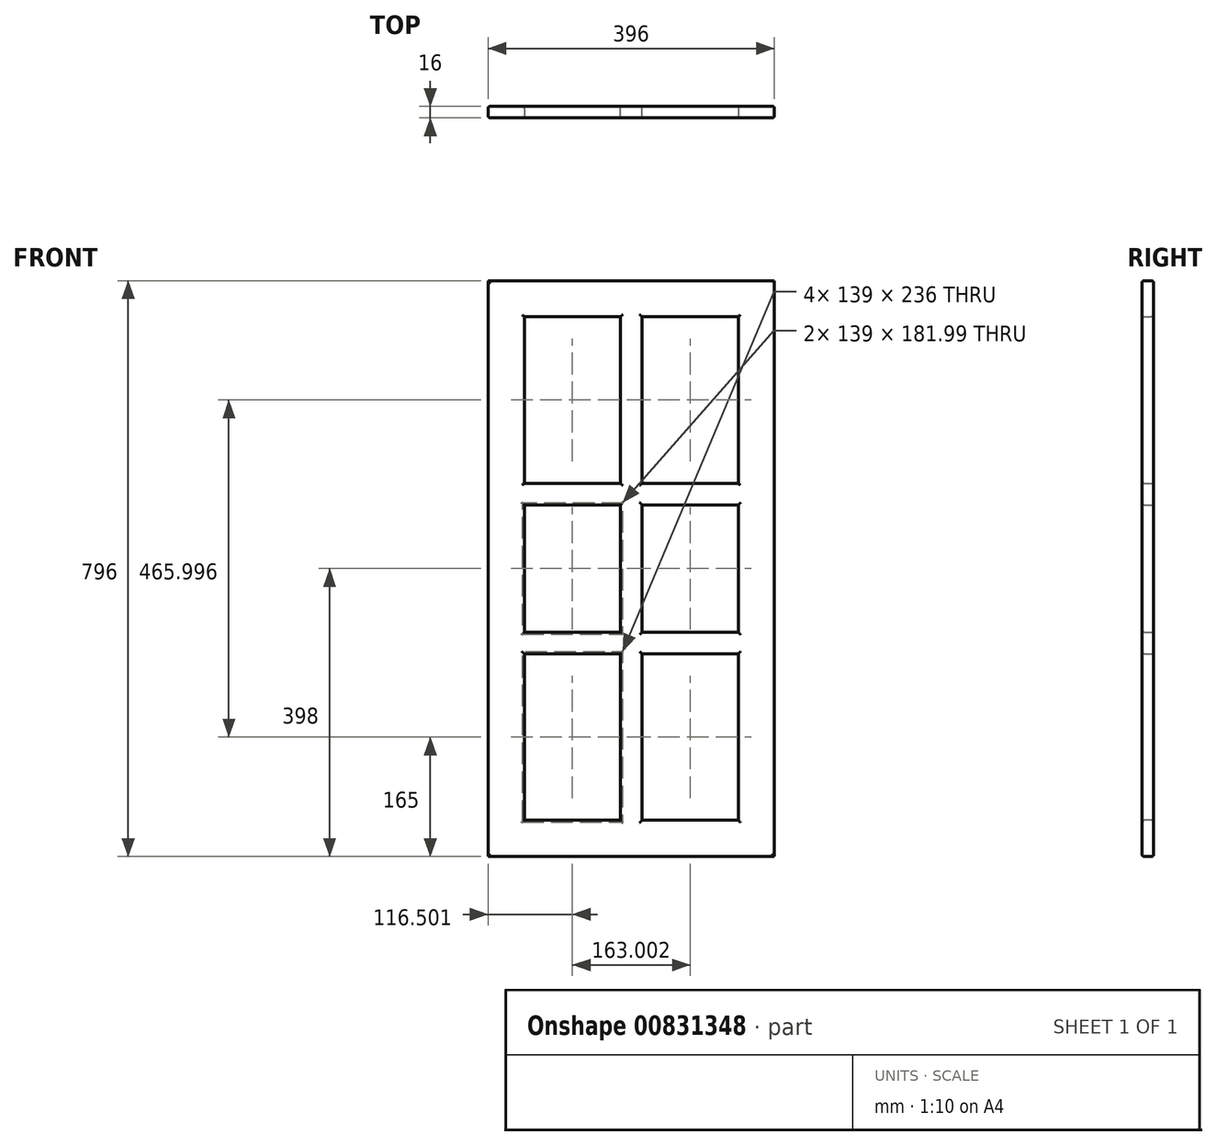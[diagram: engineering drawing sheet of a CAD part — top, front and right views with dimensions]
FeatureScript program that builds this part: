
annotation { "Feature Type Name" : "Feature", "Feature Type Description" : "" }
export const myFeature = defineFeature(function(context is Context, id is Id, definition is map)
    precondition{}
    {
        {
            var Q0;
            Q0=qCreatedBy(makeId("Front.planeOp"),FACE);
            var sketch = newSketch(context, id + "F0", { "sketchPlane" : qUnion([Q0])});
            skLineSegment(sketch, "E0.bottom", {"start": v(0, 0) * mm, "end": v(28.85, 0) * mm});
            skLineSegment(sketch, "E0.top", {"start": v(0, 37.88) * mm, "end": v(28.85, 37.88) * mm});
            skLineSegment(sketch, "E0.left", {"start": v(0, 0) * mm, "end": v(0, 37.88) * mm});
            skLineSegment(sketch, "E0.right", {"start": v(28.85, 0) * mm, "end": v(28.85, 37.88) * mm});
            skSolve(sketch);
        }
        {
            var Q0;
            Q0=makeQuery(id+"F0.imprint","IMPRINT",FACE,{"disambiguationData":[TD([[makeQuery(id+"F0.imprint","IMPRINT",EDGE,{"derivedFrom":sQuery(id+"F0.wireOp",EDGE,"E0.bottom")}),1.0]])]});
            extrude(context, id + "F1", {"entities" : qUnion([Q0]), "depth" : 16 * mm, "offsetDistance" : 25.4 * mm});
        }
        {
            var Q0;
            Q0=makeQuery(id+"F1.opExtrude","SWEPT_FACE",FACE,{"disambiguationData":[OSD([sQuery(id+"F0.wireOp",EDGE,"E0.left")])]});
            extrude(context, id + "F2", {"entities" : qUnion([Q0]), "operationType" : NewBodyOperationType.ADD, "oppositeDirection" : true, "depth" : 296 * mm, "offsetDistance" : 25.4 * mm});
        }
        {
            var Q0;
            {var subQ0=sQuery(id+"F0.wireOp",EDGE,"E0.bottom");Q0=makeQuery(id+"F2.boolean.opBoolean","MERGE",FACE,{"derivedFrom":[makeQuery(id+"F1.opExtrude","SWEPT_FACE",FACE,{"disambiguationData":[OSD([subQ0])]}),makeQuery(id+"F2.opExtrude","SWEPT_FACE",FACE,{"disambiguationData":[OSD([subQ0,sQuery(id+"F0.wireOp",EDGE,"E0.left")])]})]});}
            extrude(context, id + "F3", {"entities" : qUnion([Q0]), "operationType" : NewBodyOperationType.ADD, "oppositeDirection" : true, "depth" : 996 * mm, "offsetDistance" : 25 * mm});
        }
        {
            var Q0;
            {var subQ0=sQuery(id+"F0.wireOp",EDGE,"E0.left");var subQ1=sQuery(id+"F0.wireOp",EDGE,"E0.bottom");Q0=makeQuery(id+"F3.boolean.opBoolean","MERGE",FACE,{"derivedFrom":[makeQuery(id+"F2.boolean.opBoolean","MERGE",FACE,{"derivedFrom":[makeQuery(id+"F1.opExtrude","CAP_FACE",FACE,{"disambiguationData":[OSD([subQ1,sQuery(id+"F0.wireOp",EDGE,"E0.top"),subQ0,sQuery(id+"F0.wireOp",EDGE,"E0.right")])],"isStart":false}),makeQuery(id+"F2.opExtrude","SWEPT_FACE",FACE,{"disambiguationData":[OSD([subQ0]),TDD([makeQuery(id+"F1.opExtrude","CAP_EDGE",EDGE,{"disambiguationData":[OSD([subQ0])],"isStart":false})])]})]}),makeQuery(id+"F3.opExtrude","SWEPT_FACE",FACE,{"disambiguationData":[OSD([subQ1,subQ0]),TDD([makeQuery(id+"F2.boolean.opBoolean","MERGE",EDGE,{"derivedFrom":[makeQuery(id+"F1.opExtrude","CAP_EDGE",EDGE,{"disambiguationData":[OSD([subQ1])],"isStart":false}),makeQuery(id+"F2.opExtrude","SWEPT_EDGE",EDGE,{"disambiguationData":[OSD([subQ1,subQ0]),TDD([makeQuery(id+"F1.opExtrude","CAP_VERTEX",VERTEX,{"disambiguationData":[OSD([subQ1,subQ0])],"isStart":false})])]})]})])]})]});}
            var sketch = newSketch(context, id + "F4", { "sketchPlane" : qUnion([Q0])});
            skLineSegment(sketch, "E1.bottom", {"start": v(48.4, 906.79) * mm, "end": v(248.24, 906.79) * mm});
            skLineSegment(sketch, "E1.top", {"start": v(48.4, 105.66) * mm, "end": v(248.24, 105.66) * mm});
            skLineSegment(sketch, "E1.left", {"start": v(48.4, 906.79) * mm, "end": v(48.4, 105.66) * mm});
            skLineSegment(sketch, "E1.right", {"start": v(248.24, 906.79) * mm, "end": v(248.24, 105.66) * mm});
            skSolve(sketch);
        }
        {
            var Q0;
            Q0=makeQuery(id+"F4.imprint","IMPRINT",FACE,{"disambiguationData":[TD([[makeQuery(id+"F4.imprint","IMPRINT",EDGE,{"derivedFrom":sQuery(id+"F4.wireOp",EDGE,"E1.bottom")}),-1.0]])]});
            extrude(context, id + "F5", {"entities" : qUnion([Q0]), "operationType" : NewBodyOperationType.REMOVE, "oppositeDirection" : true, "depth" : 5 * mm, "offsetDistance" : 25 * mm});
        }
        {
            var Q0;
            Q0=makeQuery(id+"F5.boolean.opBoolean","COPY",FACE,{"derivedFrom":makeQuery(id+"F5.opExtrude","SWEPT_FACE",FACE,{"disambiguationData":[OSD([sQuery(id+"F4.wireOp",EDGE,"E1.bottom")])]})});
            extrude(context, id + "F6", {"entities" : qUnion([Q0]), "operationType" : NewBodyOperationType.REMOVE, "oppositeDirection" : true, "depth" : 39.2 * mm, "offsetDistance" : 25 * mm});
        }
        {
            var Q0;
            {var subQ0=sQuery(id+"F4.wireOp",EDGE,"E1.right");Q0=makeQuery(id+"F6.boolean.opBoolean","MERGE",FACE,{"derivedFrom":[makeQuery(id+"F5.boolean.opBoolean","COPY",FACE,{"derivedFrom":makeQuery(id+"F5.opExtrude","SWEPT_FACE",FACE,{"disambiguationData":[OSD([subQ0])]})}),makeQuery(id+"F6.opExtrude","SWEPT_FACE",FACE,{"disambiguationData":[OSD([sQuery(id+"F4.wireOp",EDGE,"E1.bottom"),subQ0])]})]});}
            extrude(context, id + "F7", {"entities" : qUnion([Q0]), "operationType" : NewBodyOperationType.ADD, "depth" : 2.24 * mm, "offsetDistance" : 25 * mm});
        }
        {
            var Q0;
            Q0=makeQuery(id+"F5.boolean.opBoolean","COPY",FACE,{"derivedFrom":makeQuery(id+"F5.opExtrude","SWEPT_FACE",FACE,{"disambiguationData":[OSD([sQuery(id+"F4.wireOp",EDGE,"E1.top")])]})});
            extrude(context, id + "F8", {"entities" : qUnion([Q0]), "operationType" : NewBodyOperationType.REMOVE, "oppositeDirection" : true, "depth" : 55.66 * mm, "offsetDistance" : 25 * mm});
        }
        {
            var Q0;
            {var subQ0=sQuery(id+"F4.wireOp",EDGE,"E1.left");Q0=makeQuery(id+"F8.boolean.opBoolean","MERGE",FACE,{"derivedFrom":[makeQuery(id+"F6.boolean.opBoolean","MERGE",FACE,{"derivedFrom":[makeQuery(id+"F5.boolean.opBoolean","COPY",FACE,{"derivedFrom":makeQuery(id+"F5.opExtrude","SWEPT_FACE",FACE,{"disambiguationData":[OSD([subQ0])]})}),makeQuery(id+"F6.opExtrude","SWEPT_FACE",FACE,{"disambiguationData":[OSD([sQuery(id+"F4.wireOp",EDGE,"E1.bottom"),subQ0])]})]}),makeQuery(id+"F8.opExtrude","SWEPT_FACE",FACE,{"disambiguationData":[OSD([sQuery(id+"F4.wireOp",EDGE,"E1.top"),subQ0])]})]});}
            extrude(context, id + "F9", {"entities" : qUnion([Q0]), "operationType" : NewBodyOperationType.ADD, "depth" : 1.59 * mm, "offsetDistance" : 25 * mm});
        }
        {
            var Q0;
            {var subQ0=sQuery(id+"F4.wireOp",EDGE,"E1.top");var subQ1=sQuery(id+"F4.wireOp",EDGE,"E1.bottom");Q0=makeQuery(id+"F8.boolean.opBoolean","MERGE",FACE,{"derivedFrom":[makeQuery(id+"F6.boolean.opBoolean","MERGE",FACE,{"derivedFrom":[makeQuery(id+"F5.boolean.opBoolean","COPY",FACE,{"derivedFrom":makeQuery(id+"F5.opExtrude","CAP_FACE",FACE,{"disambiguationData":[OSD([subQ1,subQ0,sQuery(id+"F4.wireOp",EDGE,"E1.left"),sQuery(id+"F4.wireOp",EDGE,"E1.right")])],"isStart":false})}),makeQuery(id+"F6.opExtrude","SWEPT_FACE",FACE,{"disambiguationData":[OSD([subQ1]),TDD([makeQuery(id+"F5.boolean.opBoolean","COPY",EDGE,{"derivedFrom":makeQuery(id+"F5.opExtrude","CAP_EDGE",EDGE,{"disambiguationData":[OSD([subQ1])],"isStart":false})})])]})]}),makeQuery(id+"F8.opExtrude","SWEPT_FACE",FACE,{"disambiguationData":[OSD([subQ0]),TDD([makeQuery(id+"F5.boolean.opBoolean","COPY",EDGE,{"derivedFrom":makeQuery(id+"F5.opExtrude","CAP_EDGE",EDGE,{"disambiguationData":[OSD([subQ0])],"isStart":false})})])]})]});}
            var sketch = newSketch(context, id + "F10", { "sketchPlane" : qUnion([Q0])});
            skLineSegment(sketch, "E2.bottom", {"start": v(127.14, 946) * mm, "end": v(181.91, 946) * mm});
            skLineSegment(sketch, "E2.top", {"start": v(127.14, 50) * mm, "end": v(181.91, 50) * mm});
            skLineSegment(sketch, "E2.left", {"start": v(127.14, 946) * mm, "end": v(127.14, 50) * mm});
            skLineSegment(sketch, "E2.right", {"start": v(181.91, 946) * mm, "end": v(181.91, 50) * mm});
            skSolve(sketch);
        }
        {
            var Q0;
            Q0=makeQuery(id+"F10.imprint","IMPRINT",FACE,{"disambiguationData":[TD([[makeQuery(id+"F10.imprint","IMPRINT",EDGE,{"derivedFrom":sQuery(id+"F10.wireOp",EDGE,"E2.bottom")}),-1.0]])]});
            extrude(context, id + "F11", {"entities" : qUnion([Q0]), "operationType" : NewBodyOperationType.ADD, "depth" : 5 * mm, "offsetDistance" : 25 * mm});
        }
        {
            var Q0;
            Q0=makeQuery(id+"F11.opExtrude","SWEPT_FACE",FACE,{"disambiguationData":[OSD([sQuery(id+"F10.wireOp",EDGE,"E2.left")])]});
            extrude(context, id + "F12", {"entities" : qUnion([Q0]), "operationType" : NewBodyOperationType.REMOVE, "oppositeDirection" : true, "depth" : 5.86 * mm, "offsetDistance" : 25 * mm});
        }
        {
            var Q0;
            Q0=makeQuery(id+"F11.opExtrude","SWEPT_FACE",FACE,{"disambiguationData":[OSD([sQuery(id+"F10.wireOp",EDGE,"E2.right")])]});
            extrude(context, id + "F13", {"entities" : qUnion([Q0]), "operationType" : NewBodyOperationType.REMOVE, "oppositeDirection" : true, "depth" : 18.91 * mm, "offsetDistance" : 25 * mm});
        }
        {
            var Q0;
            {var subQ0=sQuery(id+"F10.wireOp",EDGE,"E2.left");var subQ1=sQuery(id+"F4.wireOp",EDGE,"E1.bottom");var subQ2=sQuery(id+"F4.wireOp",EDGE,"E1.top");var subQ3=sQuery(id+"F4.wireOp",EDGE,"E1.left");Q0=makeQuery(id+"F12.boolean.opBoolean","MERGE",FACE,{"derivedFrom":[makeQuery(id+"F11.boolean.opBoolean","SPLIT",FACE,{"disambiguationData":[TD([makeQuery(id+"F11.opExtrude","SWEPT_FACE",FACE,{"disambiguationData":[OSD([subQ0])]})])],"derivedFrom":makeQuery(id+"F8.boolean.opBoolean","MERGE",FACE,{"derivedFrom":[makeQuery(id+"F6.boolean.opBoolean","MERGE",FACE,{"derivedFrom":[makeQuery(id+"F5.boolean.opBoolean","COPY",FACE,{"derivedFrom":makeQuery(id+"F5.opExtrude","CAP_FACE",FACE,{"disambiguationData":[OSD([subQ1,subQ2,subQ3,sQuery(id+"F4.wireOp",EDGE,"E1.right")])],"isStart":false})}),makeQuery(id+"F6.opExtrude","SWEPT_FACE",FACE,{"disambiguationData":[OSD([subQ1]),TDD([makeQuery(id+"F5.boolean.opBoolean","COPY",EDGE,{"derivedFrom":makeQuery(id+"F5.opExtrude","CAP_EDGE",EDGE,{"disambiguationData":[OSD([subQ1])],"isStart":false})})])]})]}),makeQuery(id+"F8.opExtrude","SWEPT_FACE",FACE,{"disambiguationData":[OSD([subQ2]),TDD([makeQuery(id+"F5.boolean.opBoolean","COPY",EDGE,{"derivedFrom":makeQuery(id+"F5.opExtrude","CAP_EDGE",EDGE,{"disambiguationData":[OSD([subQ2])],"isStart":false})})])]})]})}),makeQuery(id+"F12.opExtrude","SWEPT_FACE",FACE,{"disambiguationData":[OSD([subQ0]),TDD([makeQuery(id+"F11.opExtrude","CAP_EDGE",EDGE,{"disambiguationData":[OSD([subQ0])],"isStart":true})])]})]});}
            var sketch = newSketch(context, id + "F14", { "sketchPlane" : qUnion([Q0])});
            skLineSegment(sketch, "E3.bottom", {"start": v(50, 870.78) * mm, "end": v(133, 870.78) * mm});
            skLineSegment(sketch, "E3.top", {"start": v(50, 835.83) * mm, "end": v(133, 835.83) * mm});
            skLineSegment(sketch, "E3.left", {"start": v(50, 870.78) * mm, "end": v(50, 835.83) * mm});
            skLineSegment(sketch, "E3.right", {"start": v(133, 870.78) * mm, "end": v(133, 835.83) * mm});
            skLineSegment(sketch, "E4.bottom", {"start": v(50, 539.3) * mm, "end": v(133, 539.3) * mm});
            skLineSegment(sketch, "E4.top", {"start": v(50, 484.02) * mm, "end": v(133, 484.02) * mm});
            skLineSegment(sketch, "E4.left", {"start": v(50, 539.3) * mm, "end": v(50, 484.02) * mm});
            skLineSegment(sketch, "E4.right", {"start": v(133, 539.3) * mm, "end": v(133, 484.02) * mm});
            skSolve(sketch);
        }
        {
            var Q0;
            {var subQ0=sQuery(id+"F10.wireOp",EDGE,"E2.right");var subQ1=sQuery(id+"F4.wireOp",EDGE,"E1.top");var subQ2=sQuery(id+"F4.wireOp",EDGE,"E1.right");var subQ3=sQuery(id+"F4.wireOp",EDGE,"E1.bottom");Q0=makeQuery(id+"F13.boolean.opBoolean","MERGE",FACE,{"derivedFrom":[makeQuery(id+"F11.boolean.opBoolean","SPLIT",FACE,{"disambiguationData":[TD([makeQuery(id+"F11.opExtrude","SWEPT_FACE",FACE,{"disambiguationData":[OSD([subQ0])]})])],"derivedFrom":makeQuery(id+"F8.boolean.opBoolean","MERGE",FACE,{"derivedFrom":[makeQuery(id+"F6.boolean.opBoolean","MERGE",FACE,{"derivedFrom":[makeQuery(id+"F5.boolean.opBoolean","COPY",FACE,{"derivedFrom":makeQuery(id+"F5.opExtrude","CAP_FACE",FACE,{"disambiguationData":[OSD([subQ3,subQ1,sQuery(id+"F4.wireOp",EDGE,"E1.left"),subQ2])],"isStart":false})}),makeQuery(id+"F6.opExtrude","SWEPT_FACE",FACE,{"disambiguationData":[OSD([subQ3]),TDD([makeQuery(id+"F5.boolean.opBoolean","COPY",EDGE,{"derivedFrom":makeQuery(id+"F5.opExtrude","CAP_EDGE",EDGE,{"disambiguationData":[OSD([subQ3])],"isStart":false})})])]})]}),makeQuery(id+"F8.opExtrude","SWEPT_FACE",FACE,{"disambiguationData":[OSD([subQ1]),TDD([makeQuery(id+"F5.boolean.opBoolean","COPY",EDGE,{"derivedFrom":makeQuery(id+"F5.opExtrude","CAP_EDGE",EDGE,{"disambiguationData":[OSD([subQ1])],"isStart":false})})])]})]})}),makeQuery(id+"F13.opExtrude","SWEPT_FACE",FACE,{"disambiguationData":[OSD([subQ0]),TDD([makeQuery(id+"F11.opExtrude","CAP_EDGE",EDGE,{"disambiguationData":[OSD([subQ0])],"isStart":true})])]})]});}
            var sketch = newSketch(context, id + "F15", { "sketchPlane" : qUnion([Q0])});
            skLineSegment(sketch, "E5.bottom", {"start": v(163, 876.14) * mm, "end": v(246, 876.14) * mm});
            skLineSegment(sketch, "E5.top", {"start": v(163, 831.26) * mm, "end": v(246, 831.26) * mm});
            skLineSegment(sketch, "E5.left", {"start": v(163, 876.14) * mm, "end": v(163, 831.26) * mm});
            skLineSegment(sketch, "E5.right", {"start": v(246, 876.14) * mm, "end": v(246, 831.26) * mm});
            skLineSegment(sketch, "E6.bottom", {"start": v(163, 602.8) * mm, "end": v(246, 602.8) * mm});
            skLineSegment(sketch, "E6.top", {"start": v(163, 550.28) * mm, "end": v(246, 550.28) * mm});
            skLineSegment(sketch, "E6.left", {"start": v(163, 602.8) * mm, "end": v(163, 550.28) * mm});
            skLineSegment(sketch, "E6.right", {"start": v(246, 602.8) * mm, "end": v(246, 550.28) * mm});
            skSolve(sketch);
        }
        {
            var Q0;
            Q0=makeQuery(id+"F14.imprint","IMPRINT",FACE,{"disambiguationData":[TD([[makeQuery(id+"F14.imprint","IMPRINT",EDGE,{"derivedFrom":sQuery(id+"F14.wireOp",EDGE,"E3.bottom")}),-1.0]])]});
            var Q1;
            Q1=makeQuery(id+"F15.imprint","IMPRINT",FACE,{"disambiguationData":[TD([[makeQuery(id+"F15.imprint","IMPRINT",EDGE,{"derivedFrom":sQuery(id+"F15.wireOp",EDGE,"E5.bottom")}),-1.0]])]});
            var Q2;
            Q2=makeQuery(id+"F15.imprint","IMPRINT",FACE,{"disambiguationData":[TD([[makeQuery(id+"F15.imprint","IMPRINT",EDGE,{"derivedFrom":sQuery(id+"F15.wireOp",EDGE,"E6.bottom")}),-1.0]])]});
            var Q3;
            Q3=makeQuery(id+"F14.imprint","IMPRINT",FACE,{"disambiguationData":[TD([[makeQuery(id+"F14.imprint","IMPRINT",EDGE,{"derivedFrom":sQuery(id+"F14.wireOp",EDGE,"E4.bottom")}),-1.0]])]});
            extrude(context, id + "F16", {"entities" : qUnion([Q0, Q1, Q2, Q3]), "operationType" : NewBodyOperationType.ADD, "depth" : 5 * mm, "offsetDistance" : 25 * mm});
        }
        {
            var Q0;
            Q0=makeQuery(id+"F16.opExtrude","SWEPT_FACE",FACE,{"disambiguationData":[OSD([sQuery(id+"F15.wireOp",EDGE,"E6.top")])]});
            var Q1;
            Q1=makeQuery(id+"F16.opExtrude","SWEPT_FACE",FACE,{"disambiguationData":[OSD([sQuery(id+"F14.wireOp",EDGE,"E4.top")])]});
            extrude(context, id + "F17", {"entities" : qUnion([Q0, Q1]), "operationType" : NewBodyOperationType.ADD, "depth" : 300 * mm, "offsetDistance" : 25 * mm});
        }
        {
            var Q0;
            Q0=makeQuery(id+"F16.opExtrude","SWEPT_FACE",FACE,{"disambiguationData":[OSD([sQuery(id+"F14.wireOp",EDGE,"E4.bottom")])]});
            var Q1;
            Q1=makeQuery(id+"F16.opExtrude","SWEPT_FACE",FACE,{"disambiguationData":[OSD([sQuery(id+"F15.wireOp",EDGE,"E6.bottom")])]});
            extrude(context, id + "F18", {"entities" : qUnion([Q0, Q1]), "operationType" : NewBodyOperationType.REMOVE, "oppositeDirection" : true, "depth" : 300 * mm, "offsetDistance" : 25 * mm});
        }
        {
            var Q0;
            Q0=makeQuery(id+"F16.opExtrude","SWEPT_FACE",FACE,{"disambiguationData":[OSD([sQuery(id+"F14.wireOp",EDGE,"E3.top")])]});
            extrude(context, id + "F19", {"entities" : qUnion([Q0]), "operationType" : NewBodyOperationType.ADD, "depth" : 324.8 * mm, "offsetDistance" : 25 * mm});
        }
        {
            var Q0;
            Q0=makeQuery(id+"F16.opExtrude","SWEPT_FACE",FACE,{"disambiguationData":[OSD([sQuery(id+"F14.wireOp",EDGE,"E3.bottom")])]});
            extrude(context, id + "F20", {"entities" : qUnion([Q0]), "operationType" : NewBodyOperationType.REMOVE, "oppositeDirection" : true, "depth" : 324.8 * mm, "offsetDistance" : 25 * mm});
        }
        {
            var Q0;
            Q0=makeQuery(id+"F18.boolean.opBoolean","COPY",FACE,{"derivedFrom":makeQuery(id+"F18.opExtrude","CAP_FACE",FACE,{"disambiguationData":[OSD([sQuery(id+"F14.wireOp",EDGE,"E4.bottom")])],"isStart":false})});
            extrude(context, id + "F21", {"entities" : qUnion([Q0]), "operationType" : NewBodyOperationType.ADD, "depth" : 250 * mm, "offsetDistance" : 25 * mm});
        }
        {
            var Q0;
            Q0=makeQuery(id+"F17.opExtrude","CAP_FACE",FACE,{"disambiguationData":[OSD([sQuery(id+"F14.wireOp",EDGE,"E4.top")])],"isStart":false});
            extrude(context, id + "F22", {"entities" : qUnion([Q0]), "operationType" : NewBodyOperationType.REMOVE, "oppositeDirection" : true, "depth" : 250 * mm, "offsetDistance" : 25 * mm});
        }
        {
            var Q0;
            Q0=makeQuery(id+"F20.boolean.opBoolean","COPY",FACE,{"derivedFrom":makeQuery(id+"F20.opExtrude","CAP_FACE",FACE,{"disambiguationData":[OSD([sQuery(id+"F14.wireOp",EDGE,"E3.bottom")])],"isStart":false})});
            extrude(context, id + "F23", {"entities" : qUnion([Q0]), "operationType" : NewBodyOperationType.ADD, "depth" : 100 * mm, "offsetDistance" : 25 * mm});
        }
        {
            var Q0;
            Q0=makeQuery(id+"F19.opExtrude","CAP_FACE",FACE,{"disambiguationData":[OSD([sQuery(id+"F14.wireOp",EDGE,"E3.top")])],"isStart":false});
            extrude(context, id + "F24", {"entities" : qUnion([Q0]), "operationType" : NewBodyOperationType.REMOVE, "oppositeDirection" : true, "depth" : 100 * mm, "offsetDistance" : 25 * mm});
        }
        {
            var Q0;
            Q0=makeQuery(id+"F23.opExtrude","CAP_FACE",FACE,{"disambiguationData":[OSD([sQuery(id+"F14.wireOp",EDGE,"E3.bottom")])],"isStart":false});
            extrude(context, id + "F25", {"entities" : qUnion([Q0]), "operationType" : NewBodyOperationType.ADD, "depth" : 50 * mm, "offsetDistance" : 25 * mm});
        }
        {
            var Q0;
            Q0=makeQuery(id+"F24.boolean.opBoolean","COPY",FACE,{"derivedFrom":makeQuery(id+"F24.opExtrude","CAP_FACE",FACE,{"disambiguationData":[OSD([sQuery(id+"F14.wireOp",EDGE,"E3.top")])],"isStart":false})});
            extrude(context, id + "F26", {"entities" : qUnion([Q0]), "operationType" : NewBodyOperationType.REMOVE, "oppositeDirection" : true, "depth" : 50 * mm, "offsetDistance" : 25 * mm});
        }
        {
            var Q0;
            Q0=makeQuery(id+"F22.boolean.opBoolean","COPY",FACE,{"derivedFrom":makeQuery(id+"F22.opExtrude","CAP_FACE",FACE,{"disambiguationData":[OSD([sQuery(id+"F14.wireOp",EDGE,"E4.top")])],"isStart":false})});
            extrude(context, id + "F27", {"entities" : qUnion([Q0]), "operationType" : NewBodyOperationType.ADD, "depth" : 134.02 * mm, "offsetDistance" : 25 * mm});
        }
        {
            var Q0;
            Q0=makeQuery(id+"F27.opExtrude","CAP_FACE",FACE,{"disambiguationData":[OSD([sQuery(id+"F14.wireOp",EDGE,"E4.top")])],"isStart":false});
            extrude(context, id + "F28", {"entities" : qUnion([Q0]), "operationType" : NewBodyOperationType.REMOVE, "oppositeDirection" : true, "depth" : 100 * mm, "offsetDistance" : 25 * mm});
        }
        {
            var Q0;
            Q0=makeQuery(id+"F26.boolean.opBoolean","COPY",FACE,{"derivedFrom":makeQuery(id+"F26.opExtrude","CAP_FACE",FACE,{"disambiguationData":[OSD([sQuery(id+"F14.wireOp",EDGE,"E3.top")])],"isStart":false})});
            extrude(context, id + "F29", {"entities" : qUnion([Q0]), "operationType" : NewBodyOperationType.ADD, "depth" : 100 * mm, "offsetDistance" : 25 * mm});
        }
        {
            var Q0;
            Q0=makeQuery(id+"F25.opExtrude","CAP_FACE",FACE,{"disambiguationData":[OSD([sQuery(id+"F14.wireOp",EDGE,"E3.bottom")])],"isStart":false});
            extrude(context, id + "F30", {"entities" : qUnion([Q0]), "operationType" : NewBodyOperationType.REMOVE, "oppositeDirection" : true, "depth" : 100 * mm, "offsetDistance" : 25 * mm});
        }
        {
            var Q0;
            Q0=makeQuery(id+"F30.boolean.opBoolean","COPY",FACE,{"derivedFrom":makeQuery(id+"F30.opExtrude","CAP_FACE",FACE,{"disambiguationData":[OSD([sQuery(id+"F14.wireOp",EDGE,"E3.bottom")])],"isStart":false})});
            extrude(context, id + "F31", {"entities" : qUnion([Q0]), "operationType" : NewBodyOperationType.ADD, "depth" : 50 * mm, "offsetDistance" : 25 * mm});
        }
        {
            var Q0;
            Q0=makeQuery(id+"F29.opExtrude","CAP_FACE",FACE,{"disambiguationData":[OSD([sQuery(id+"F14.wireOp",EDGE,"E3.top")])],"isStart":false});
            extrude(context, id + "F32", {"entities" : qUnion([Q0]), "operationType" : NewBodyOperationType.REMOVE, "oppositeDirection" : true, "depth" : 54.95 * mm, "offsetDistance" : 25 * mm});
        }
        {
            var Q0;
            Q0=makeQuery(id+"F28.boolean.opBoolean","COPY",FACE,{"derivedFrom":makeQuery(id+"F28.opExtrude","CAP_FACE",FACE,{"disambiguationData":[OSD([sQuery(id+"F14.wireOp",EDGE,"E4.top")])],"isStart":false})});
            extrude(context, id + "F33", {"entities" : qUnion([Q0]), "operationType" : NewBodyOperationType.ADD, "depth" : 50 * mm, "offsetDistance" : 25 * mm});
        }
        {
            var Q0;
            Q0=makeQuery(id+"F21.opExtrude","CAP_FACE",FACE,{"disambiguationData":[OSD([sQuery(id+"F14.wireOp",EDGE,"E4.bottom")])],"isStart":false});
            extrude(context, id + "F34", {"entities" : qUnion([Q0]), "operationType" : NewBodyOperationType.REMOVE, "oppositeDirection" : true, "depth" : 109.3 * mm, "offsetDistance" : 25 * mm});
        }
        {
            var Q0;
            Q0=makeQuery(id+"F16.opExtrude","SWEPT_FACE",FACE,{"disambiguationData":[OSD([sQuery(id+"F15.wireOp",EDGE,"E5.top")])]});
            extrude(context, id + "F35", {"entities" : qUnion([Q0]), "operationType" : NewBodyOperationType.REMOVE, "oppositeDirection" : true, "depth" : 14.88 * mm, "offsetDistance" : 25 * mm});
        }
        {
            var Q0;
            Q0=makeQuery(id+"F35.boolean.opBoolean","COPY",FACE,{"derivedFrom":makeQuery(id+"F35.opExtrude","CAP_FACE",FACE,{"disambiguationData":[OSD([sQuery(id+"F15.wireOp",EDGE,"E5.top")])],"isStart":false})});
            extrude(context, id + "F36", {"entities" : qUnion([Q0]), "operationType" : NewBodyOperationType.ADD, "depth" : 230.15 * mm, "offsetDistance" : 25 * mm});
        }
        {
            var Q0;
            Q0=makeQuery(id+"F16.opExtrude","SWEPT_FACE",FACE,{"disambiguationData":[OSD([sQuery(id+"F15.wireOp",EDGE,"E5.bottom")])]});
            extrude(context, id + "F37", {"entities" : qUnion([Q0]), "operationType" : NewBodyOperationType.REMOVE, "oppositeDirection" : true, "depth" : 230.15 * mm, "offsetDistance" : 25 * mm});
        }
        {
            var Q0;
            Q0=makeQuery(id+"F17.opExtrude","CAP_FACE",FACE,{"disambiguationData":[OSD([sQuery(id+"F15.wireOp",EDGE,"E6.top")])],"isStart":false});
            extrude(context, id + "F38", {"entities" : qUnion([Q0]), "operationType" : NewBodyOperationType.REMOVE, "oppositeDirection" : true, "depth" : 22.52 * mm, "offsetDistance" : 25 * mm});
        }
        {
            var Q0;
            Q0=makeQuery(id+"F18.boolean.opBoolean","COPY",FACE,{"derivedFrom":makeQuery(id+"F18.opExtrude","CAP_FACE",FACE,{"disambiguationData":[OSD([sQuery(id+"F15.wireOp",EDGE,"E6.bottom")])],"isStart":false})});
            extrude(context, id + "F39", {"entities" : qUnion([Q0]), "operationType" : NewBodyOperationType.ADD, "depth" : 77.2 * mm, "offsetDistance" : 25 * mm});
        }
        {
            var Q0;
            Q0=makeQuery(id+"F38.boolean.opBoolean","COPY",FACE,{"derivedFrom":makeQuery(id+"F38.opExtrude","CAP_FACE",FACE,{"disambiguationData":[OSD([sQuery(id+"F15.wireOp",EDGE,"E6.top")])],"isStart":false})});
            extrude(context, id + "F40", {"entities" : qUnion([Q0]), "operationType" : NewBodyOperationType.REMOVE, "oppositeDirection" : true, "depth" : 77.2 * mm, "offsetDistance" : 25 * mm});
        }
        {
            var Q0;
            {var subQ0=sQuery(id+"F14.wireOp",EDGE,"E3.bottom");var subQ1=makeQuery(id+"F16.opExtrude","CAP_EDGE",EDGE,{"disambiguationData":[OSD([subQ0])],"isStart":true});var subQ2=sQuery(id+"F10.wireOp",EDGE,"E2.left");var subQ3=sQuery(id+"F4.wireOp",EDGE,"E1.bottom");var subQ4=sQuery(id+"F4.wireOp",EDGE,"E1.left");var subQ5=sQuery(id+"F4.wireOp",EDGE,"E1.top");var subQ7=makeQuery(id+"F6.boolean.opBoolean","COPY",FACE,{"derivedFrom":makeQuery(id+"F6.opExtrude","CAP_FACE",FACE,{"disambiguationData":[OSD([subQ3])],"isStart":false})});Q0=makeQuery(id+"F30.boolean.opBoolean","MERGE",FACE,{"derivedFrom":[makeQuery(id+"F20.boolean.opBoolean","MERGE",FACE,{"derivedFrom":[makeQuery(id+"F16.boolean.opBoolean","SPLIT",FACE,{"disambiguationData":[TD([subQ7])],"derivedFrom":makeQuery(id+"F12.boolean.opBoolean","MERGE",FACE,{"derivedFrom":[makeQuery(id+"F11.boolean.opBoolean","SPLIT",FACE,{"disambiguationData":[TD([makeQuery(id+"F11.opExtrude","SWEPT_FACE",FACE,{"disambiguationData":[OSD([subQ2])]})])],"derivedFrom":makeQuery(id+"F8.boolean.opBoolean","MERGE",FACE,{"derivedFrom":[makeQuery(id+"F6.boolean.opBoolean","MERGE",FACE,{"derivedFrom":[makeQuery(id+"F5.boolean.opBoolean","COPY",FACE,{"derivedFrom":makeQuery(id+"F5.opExtrude","CAP_FACE",FACE,{"disambiguationData":[OSD([subQ3,subQ5,subQ4,sQuery(id+"F4.wireOp",EDGE,"E1.right")])],"isStart":false})}),makeQuery(id+"F6.opExtrude","SWEPT_FACE",FACE,{"disambiguationData":[OSD([subQ3]),TDD([makeQuery(id+"F5.boolean.opBoolean","COPY",EDGE,{"derivedFrom":makeQuery(id+"F5.opExtrude","CAP_EDGE",EDGE,{"disambiguationData":[OSD([subQ3])],"isStart":false})})])]})]}),makeQuery(id+"F8.opExtrude","SWEPT_FACE",FACE,{"disambiguationData":[OSD([subQ5]),TDD([makeQuery(id+"F5.boolean.opBoolean","COPY",EDGE,{"derivedFrom":makeQuery(id+"F5.opExtrude","CAP_EDGE",EDGE,{"disambiguationData":[OSD([subQ5])],"isStart":false})})])]})]})}),makeQuery(id+"F12.opExtrude","SWEPT_FACE",FACE,{"disambiguationData":[OSD([subQ2]),TDD([makeQuery(id+"F11.opExtrude","CAP_EDGE",EDGE,{"disambiguationData":[OSD([subQ2])],"isStart":true})])]})]})}),makeQuery(id+"F20.opExtrude","SWEPT_FACE",FACE,{"disambiguationData":[OSD([subQ0]),TDD([subQ1])]})]}),makeQuery(id+"F30.opExtrude","SWEPT_FACE",FACE,{"disambiguationData":[OSD([subQ0]),TDD([makeQuery(id+"F25.opExtrude","CAP_EDGE",EDGE,{"disambiguationData":[OSD([subQ0]),TDD([makeQuery(id+"F23.opExtrude","CAP_EDGE",EDGE,{"disambiguationData":[OSD([subQ0]),TDD([makeQuery(id+"F20.boolean.opBoolean","COPY",EDGE,{"derivedFrom":makeQuery(id+"F20.opExtrude","CAP_EDGE",EDGE,{"disambiguationData":[OSD([subQ0]),TDD([subQ1])],"isStart":false})})])],"isStart":false})])],"isStart":false})])]})]});}
            var Q1;
            {var subQ0=sQuery(id+"F15.wireOp",EDGE,"E5.bottom");var subQ1=sQuery(id+"F10.wireOp",EDGE,"E2.right");var subQ2=sQuery(id+"F4.wireOp",EDGE,"E1.bottom");var subQ3=sQuery(id+"F4.wireOp",EDGE,"E1.right");var subQ4=sQuery(id+"F4.wireOp",EDGE,"E1.top");var subQ7=makeQuery(id+"F6.boolean.opBoolean","COPY",FACE,{"derivedFrom":makeQuery(id+"F6.opExtrude","CAP_FACE",FACE,{"disambiguationData":[OSD([subQ2])],"isStart":false})});Q1=makeQuery(id+"F37.boolean.opBoolean","MERGE",FACE,{"derivedFrom":[makeQuery(id+"F16.boolean.opBoolean","SPLIT",FACE,{"disambiguationData":[TD([subQ7])],"derivedFrom":makeQuery(id+"F13.boolean.opBoolean","MERGE",FACE,{"derivedFrom":[makeQuery(id+"F11.boolean.opBoolean","SPLIT",FACE,{"disambiguationData":[TD([makeQuery(id+"F11.opExtrude","SWEPT_FACE",FACE,{"disambiguationData":[OSD([subQ1])]})])],"derivedFrom":makeQuery(id+"F8.boolean.opBoolean","MERGE",FACE,{"derivedFrom":[makeQuery(id+"F6.boolean.opBoolean","MERGE",FACE,{"derivedFrom":[makeQuery(id+"F5.boolean.opBoolean","COPY",FACE,{"derivedFrom":makeQuery(id+"F5.opExtrude","CAP_FACE",FACE,{"disambiguationData":[OSD([subQ2,subQ4,sQuery(id+"F4.wireOp",EDGE,"E1.left"),subQ3])],"isStart":false})}),makeQuery(id+"F6.opExtrude","SWEPT_FACE",FACE,{"disambiguationData":[OSD([subQ2]),TDD([makeQuery(id+"F5.boolean.opBoolean","COPY",EDGE,{"derivedFrom":makeQuery(id+"F5.opExtrude","CAP_EDGE",EDGE,{"disambiguationData":[OSD([subQ2])],"isStart":false})})])]})]}),makeQuery(id+"F8.opExtrude","SWEPT_FACE",FACE,{"disambiguationData":[OSD([subQ4]),TDD([makeQuery(id+"F5.boolean.opBoolean","COPY",EDGE,{"derivedFrom":makeQuery(id+"F5.opExtrude","CAP_EDGE",EDGE,{"disambiguationData":[OSD([subQ4])],"isStart":false})})])]})]})}),makeQuery(id+"F13.opExtrude","SWEPT_FACE",FACE,{"disambiguationData":[OSD([subQ1]),TDD([makeQuery(id+"F11.opExtrude","CAP_EDGE",EDGE,{"disambiguationData":[OSD([subQ1])],"isStart":true})])]})]})}),makeQuery(id+"F37.opExtrude","SWEPT_FACE",FACE,{"disambiguationData":[OSD([subQ0]),TDD([makeQuery(id+"F16.opExtrude","CAP_EDGE",EDGE,{"disambiguationData":[OSD([subQ0])],"isStart":true})])]})]});}
            var Q2;
            {var subQ0=sQuery(id+"F15.wireOp",EDGE,"E5.top");var subQ1=sQuery(id+"F15.wireOp",EDGE,"E6.bottom");var subQ2=sQuery(id+"F10.wireOp",EDGE,"E2.right");var subQ3=sQuery(id+"F4.wireOp",EDGE,"E1.right");var subQ4=sQuery(id+"F4.wireOp",EDGE,"E1.top");var subQ6=sQuery(id+"F4.wireOp",EDGE,"E1.bottom");Q2=makeQuery(id+"F35.boolean.opBoolean","MERGE",FACE,{"derivedFrom":[makeQuery(id+"F18.boolean.opBoolean","MERGE",FACE,{"derivedFrom":[makeQuery(id+"F16.boolean.opBoolean","SPLIT",FACE,{"disambiguationData":[TD([makeQuery(id+"F16.opExtrude","SWEPT_FACE",FACE,{"disambiguationData":[OSD([subQ0])]})])],"derivedFrom":makeQuery(id+"F13.boolean.opBoolean","MERGE",FACE,{"derivedFrom":[makeQuery(id+"F11.boolean.opBoolean","SPLIT",FACE,{"disambiguationData":[TD([makeQuery(id+"F11.opExtrude","SWEPT_FACE",FACE,{"disambiguationData":[OSD([subQ2])]})])],"derivedFrom":makeQuery(id+"F8.boolean.opBoolean","MERGE",FACE,{"derivedFrom":[makeQuery(id+"F6.boolean.opBoolean","MERGE",FACE,{"derivedFrom":[makeQuery(id+"F5.boolean.opBoolean","COPY",FACE,{"derivedFrom":makeQuery(id+"F5.opExtrude","CAP_FACE",FACE,{"disambiguationData":[OSD([subQ6,subQ4,sQuery(id+"F4.wireOp",EDGE,"E1.left"),subQ3])],"isStart":false})}),makeQuery(id+"F6.opExtrude","SWEPT_FACE",FACE,{"disambiguationData":[OSD([subQ6]),TDD([makeQuery(id+"F5.boolean.opBoolean","COPY",EDGE,{"derivedFrom":makeQuery(id+"F5.opExtrude","CAP_EDGE",EDGE,{"disambiguationData":[OSD([subQ6])],"isStart":false})})])]})]}),makeQuery(id+"F8.opExtrude","SWEPT_FACE",FACE,{"disambiguationData":[OSD([subQ4]),TDD([makeQuery(id+"F5.boolean.opBoolean","COPY",EDGE,{"derivedFrom":makeQuery(id+"F5.opExtrude","CAP_EDGE",EDGE,{"disambiguationData":[OSD([subQ4])],"isStart":false})})])]})]})}),makeQuery(id+"F13.opExtrude","SWEPT_FACE",FACE,{"disambiguationData":[OSD([subQ2]),TDD([makeQuery(id+"F11.opExtrude","CAP_EDGE",EDGE,{"disambiguationData":[OSD([subQ2])],"isStart":true})])]})]})}),makeQuery(id+"F18.opExtrude","SWEPT_FACE",FACE,{"disambiguationData":[OSD([subQ1]),TDD([makeQuery(id+"F16.opExtrude","CAP_EDGE",EDGE,{"disambiguationData":[OSD([subQ1])],"isStart":true})])]})]}),makeQuery(id+"F35.opExtrude","SWEPT_FACE",FACE,{"disambiguationData":[OSD([subQ0]),TDD([makeQuery(id+"F16.opExtrude","CAP_EDGE",EDGE,{"disambiguationData":[OSD([subQ0])],"isStart":true})])]})]});}
            var Q3;
            {var subQ0=sQuery(id+"F14.wireOp",EDGE,"E4.bottom");var subQ1=makeQuery(id+"F16.opExtrude","CAP_EDGE",EDGE,{"disambiguationData":[OSD([subQ0])],"isStart":true});var subQ2=sQuery(id+"F14.wireOp",EDGE,"E3.top");var subQ3=makeQuery(id+"F19.opExtrude","CAP_EDGE",EDGE,{"disambiguationData":[OSD([subQ2]),TDD([makeQuery(id+"F16.opExtrude","CAP_EDGE",EDGE,{"disambiguationData":[OSD([subQ2])],"isStart":true})])],"isStart":false});var subQ4=makeQuery(id+"F24.boolean.opBoolean","COPY",EDGE,{"derivedFrom":makeQuery(id+"F24.opExtrude","CAP_EDGE",EDGE,{"disambiguationData":[OSD([subQ2]),TDD([subQ3])],"isStart":false})});var subQ5=sQuery(id+"F4.wireOp",EDGE,"E1.left");var subQ6=sQuery(id+"F4.wireOp",EDGE,"E1.top");var subQ7=sQuery(id+"F4.wireOp",EDGE,"E1.bottom");var subQ9=sQuery(id+"F10.wireOp",EDGE,"E2.left");Q3=makeQuery(id+"F34.boolean.opBoolean","MERGE",FACE,{"derivedFrom":[makeQuery(id+"F32.boolean.opBoolean","MERGE",FACE,{"derivedFrom":[makeQuery(id+"F26.boolean.opBoolean","MERGE",FACE,{"derivedFrom":[makeQuery(id+"F24.boolean.opBoolean","MERGE",FACE,{"derivedFrom":[makeQuery(id+"F18.boolean.opBoolean","MERGE",FACE,{"derivedFrom":[makeQuery(id+"F16.boolean.opBoolean","SPLIT",FACE,{"disambiguationData":[TD([makeQuery(id+"F16.opExtrude","SWEPT_FACE",FACE,{"disambiguationData":[OSD([subQ2])]})])],"derivedFrom":makeQuery(id+"F12.boolean.opBoolean","MERGE",FACE,{"derivedFrom":[makeQuery(id+"F11.boolean.opBoolean","SPLIT",FACE,{"disambiguationData":[TD([makeQuery(id+"F11.opExtrude","SWEPT_FACE",FACE,{"disambiguationData":[OSD([subQ9])]})])],"derivedFrom":makeQuery(id+"F8.boolean.opBoolean","MERGE",FACE,{"derivedFrom":[makeQuery(id+"F6.boolean.opBoolean","MERGE",FACE,{"derivedFrom":[makeQuery(id+"F5.boolean.opBoolean","COPY",FACE,{"derivedFrom":makeQuery(id+"F5.opExtrude","CAP_FACE",FACE,{"disambiguationData":[OSD([subQ7,subQ6,subQ5,sQuery(id+"F4.wireOp",EDGE,"E1.right")])],"isStart":false})}),makeQuery(id+"F6.opExtrude","SWEPT_FACE",FACE,{"disambiguationData":[OSD([subQ7]),TDD([makeQuery(id+"F5.boolean.opBoolean","COPY",EDGE,{"derivedFrom":makeQuery(id+"F5.opExtrude","CAP_EDGE",EDGE,{"disambiguationData":[OSD([subQ7])],"isStart":false})})])]})]}),makeQuery(id+"F8.opExtrude","SWEPT_FACE",FACE,{"disambiguationData":[OSD([subQ6]),TDD([makeQuery(id+"F5.boolean.opBoolean","COPY",EDGE,{"derivedFrom":makeQuery(id+"F5.opExtrude","CAP_EDGE",EDGE,{"disambiguationData":[OSD([subQ6])],"isStart":false})})])]})]})}),makeQuery(id+"F12.opExtrude","SWEPT_FACE",FACE,{"disambiguationData":[OSD([subQ9]),TDD([makeQuery(id+"F11.opExtrude","CAP_EDGE",EDGE,{"disambiguationData":[OSD([subQ9])],"isStart":true})])]})]})}),makeQuery(id+"F18.opExtrude","SWEPT_FACE",FACE,{"disambiguationData":[OSD([subQ0]),TDD([subQ1])]})]}),makeQuery(id+"F24.opExtrude","SWEPT_FACE",FACE,{"disambiguationData":[OSD([subQ2]),TDD([subQ3])]})]}),makeQuery(id+"F26.opExtrude","SWEPT_FACE",FACE,{"disambiguationData":[OSD([subQ2]),TDD([subQ4])]})]}),makeQuery(id+"F32.opExtrude","SWEPT_FACE",FACE,{"disambiguationData":[OSD([subQ2]),TDD([makeQuery(id+"F29.opExtrude","CAP_EDGE",EDGE,{"disambiguationData":[OSD([subQ2]),TDD([makeQuery(id+"F26.boolean.opBoolean","COPY",EDGE,{"derivedFrom":makeQuery(id+"F26.opExtrude","CAP_EDGE",EDGE,{"disambiguationData":[OSD([subQ2]),TDD([subQ4])],"isStart":false})})])],"isStart":false})])]})]}),makeQuery(id+"F34.opExtrude","SWEPT_FACE",FACE,{"disambiguationData":[OSD([subQ0]),TDD([makeQuery(id+"F21.opExtrude","CAP_EDGE",EDGE,{"disambiguationData":[OSD([subQ0]),TDD([makeQuery(id+"F18.boolean.opBoolean","COPY",EDGE,{"derivedFrom":makeQuery(id+"F18.opExtrude","CAP_EDGE",EDGE,{"disambiguationData":[OSD([subQ0]),TDD([subQ1])],"isStart":false})})])],"isStart":false})])]})]});}
            var Q4;
            {var subQ0=sQuery(id+"F14.wireOp",EDGE,"E4.top");var subQ1=makeQuery(id+"F17.opExtrude","CAP_EDGE",EDGE,{"disambiguationData":[OSD([subQ0]),TDD([makeQuery(id+"F16.opExtrude","CAP_EDGE",EDGE,{"disambiguationData":[OSD([subQ0])],"isStart":true})])],"isStart":false});var subQ2=sQuery(id+"F10.wireOp",EDGE,"E2.left");var subQ3=sQuery(id+"F4.wireOp",EDGE,"E1.top");var subQ4=sQuery(id+"F4.wireOp",EDGE,"E1.left");var subQ5=sQuery(id+"F4.wireOp",EDGE,"E1.bottom");var subQ7=makeQuery(id+"F8.boolean.opBoolean","COPY",FACE,{"derivedFrom":makeQuery(id+"F8.opExtrude","CAP_FACE",FACE,{"disambiguationData":[OSD([subQ3])],"isStart":false})});Q4=makeQuery(id+"F28.boolean.opBoolean","MERGE",FACE,{"derivedFrom":[makeQuery(id+"F22.boolean.opBoolean","MERGE",FACE,{"derivedFrom":[makeQuery(id+"F16.boolean.opBoolean","SPLIT",FACE,{"disambiguationData":[TD([subQ7])],"derivedFrom":makeQuery(id+"F12.boolean.opBoolean","MERGE",FACE,{"derivedFrom":[makeQuery(id+"F11.boolean.opBoolean","SPLIT",FACE,{"disambiguationData":[TD([makeQuery(id+"F11.opExtrude","SWEPT_FACE",FACE,{"disambiguationData":[OSD([subQ2])]})])],"derivedFrom":makeQuery(id+"F8.boolean.opBoolean","MERGE",FACE,{"derivedFrom":[makeQuery(id+"F6.boolean.opBoolean","MERGE",FACE,{"derivedFrom":[makeQuery(id+"F5.boolean.opBoolean","COPY",FACE,{"derivedFrom":makeQuery(id+"F5.opExtrude","CAP_FACE",FACE,{"disambiguationData":[OSD([subQ5,subQ3,subQ4,sQuery(id+"F4.wireOp",EDGE,"E1.right")])],"isStart":false})}),makeQuery(id+"F6.opExtrude","SWEPT_FACE",FACE,{"disambiguationData":[OSD([subQ5]),TDD([makeQuery(id+"F5.boolean.opBoolean","COPY",EDGE,{"derivedFrom":makeQuery(id+"F5.opExtrude","CAP_EDGE",EDGE,{"disambiguationData":[OSD([subQ5])],"isStart":false})})])]})]}),makeQuery(id+"F8.opExtrude","SWEPT_FACE",FACE,{"disambiguationData":[OSD([subQ3]),TDD([makeQuery(id+"F5.boolean.opBoolean","COPY",EDGE,{"derivedFrom":makeQuery(id+"F5.opExtrude","CAP_EDGE",EDGE,{"disambiguationData":[OSD([subQ3])],"isStart":false})})])]})]})}),makeQuery(id+"F12.opExtrude","SWEPT_FACE",FACE,{"disambiguationData":[OSD([subQ2]),TDD([makeQuery(id+"F11.opExtrude","CAP_EDGE",EDGE,{"disambiguationData":[OSD([subQ2])],"isStart":true})])]})]})}),makeQuery(id+"F22.opExtrude","SWEPT_FACE",FACE,{"disambiguationData":[OSD([subQ0]),TDD([subQ1])]})]}),makeQuery(id+"F28.opExtrude","SWEPT_FACE",FACE,{"disambiguationData":[OSD([subQ0]),TDD([makeQuery(id+"F27.opExtrude","CAP_EDGE",EDGE,{"disambiguationData":[OSD([subQ0]),TDD([makeQuery(id+"F22.boolean.opBoolean","COPY",EDGE,{"derivedFrom":makeQuery(id+"F22.opExtrude","CAP_EDGE",EDGE,{"disambiguationData":[OSD([subQ0]),TDD([subQ1])],"isStart":false})})])],"isStart":false})])]})]});}
            var Q5;
            {var subQ0=sQuery(id+"F15.wireOp",EDGE,"E6.top");var subQ1=makeQuery(id+"F17.opExtrude","CAP_EDGE",EDGE,{"disambiguationData":[OSD([subQ0]),TDD([makeQuery(id+"F16.opExtrude","CAP_EDGE",EDGE,{"disambiguationData":[OSD([subQ0])],"isStart":true})])],"isStart":false});var subQ2=sQuery(id+"F10.wireOp",EDGE,"E2.right");var subQ3=sQuery(id+"F4.wireOp",EDGE,"E1.top");var subQ4=makeQuery(id+"F8.boolean.opBoolean","COPY",FACE,{"derivedFrom":makeQuery(id+"F8.opExtrude","CAP_FACE",FACE,{"disambiguationData":[OSD([subQ3])],"isStart":false})});var subQ5=sQuery(id+"F4.wireOp",EDGE,"E1.right");var subQ7=sQuery(id+"F4.wireOp",EDGE,"E1.bottom");Q5=makeQuery(id+"F40.boolean.opBoolean","MERGE",FACE,{"derivedFrom":[makeQuery(id+"F38.boolean.opBoolean","MERGE",FACE,{"derivedFrom":[makeQuery(id+"F16.boolean.opBoolean","SPLIT",FACE,{"disambiguationData":[TD([subQ4])],"derivedFrom":makeQuery(id+"F13.boolean.opBoolean","MERGE",FACE,{"derivedFrom":[makeQuery(id+"F11.boolean.opBoolean","SPLIT",FACE,{"disambiguationData":[TD([makeQuery(id+"F11.opExtrude","SWEPT_FACE",FACE,{"disambiguationData":[OSD([subQ2])]})])],"derivedFrom":makeQuery(id+"F8.boolean.opBoolean","MERGE",FACE,{"derivedFrom":[makeQuery(id+"F6.boolean.opBoolean","MERGE",FACE,{"derivedFrom":[makeQuery(id+"F5.boolean.opBoolean","COPY",FACE,{"derivedFrom":makeQuery(id+"F5.opExtrude","CAP_FACE",FACE,{"disambiguationData":[OSD([subQ7,subQ3,sQuery(id+"F4.wireOp",EDGE,"E1.left"),subQ5])],"isStart":false})}),makeQuery(id+"F6.opExtrude","SWEPT_FACE",FACE,{"disambiguationData":[OSD([subQ7]),TDD([makeQuery(id+"F5.boolean.opBoolean","COPY",EDGE,{"derivedFrom":makeQuery(id+"F5.opExtrude","CAP_EDGE",EDGE,{"disambiguationData":[OSD([subQ7])],"isStart":false})})])]})]}),makeQuery(id+"F8.opExtrude","SWEPT_FACE",FACE,{"disambiguationData":[OSD([subQ3]),TDD([makeQuery(id+"F5.boolean.opBoolean","COPY",EDGE,{"derivedFrom":makeQuery(id+"F5.opExtrude","CAP_EDGE",EDGE,{"disambiguationData":[OSD([subQ3])],"isStart":false})})])]})]})}),makeQuery(id+"F13.opExtrude","SWEPT_FACE",FACE,{"disambiguationData":[OSD([subQ2]),TDD([makeQuery(id+"F11.opExtrude","CAP_EDGE",EDGE,{"disambiguationData":[OSD([subQ2])],"isStart":true})])]})]})}),makeQuery(id+"F38.opExtrude","SWEPT_FACE",FACE,{"disambiguationData":[OSD([subQ0]),TDD([subQ1])]})]}),makeQuery(id+"F40.opExtrude","SWEPT_FACE",FACE,{"disambiguationData":[OSD([subQ0]),TDD([makeQuery(id+"F38.boolean.opBoolean","COPY",EDGE,{"derivedFrom":makeQuery(id+"F38.opExtrude","CAP_EDGE",EDGE,{"disambiguationData":[OSD([subQ0]),TDD([subQ1])],"isStart":false})})])]})]});}
            extrude(context, id + "F41", {"entities" : qUnion([Q0, Q1, Q2, Q3, Q4, Q5]), "operationType" : NewBodyOperationType.REMOVE, "oppositeDirection" : true, "depth" : 11 * mm, "offsetDistance" : 25 * mm});
        }
        {
            var Q0;
            {var subQ0=sQuery(id+"F15.wireOp",EDGE,"E5.top");Q0=makeQuery(id+"F41.boolean.opBoolean","MERGE",FACE,{"derivedFrom":[makeQuery(id+"F36.opExtrude","CAP_FACE",FACE,{"disambiguationData":[OSD([subQ0])],"isStart":false}),makeQuery(id+"F41.opExtrude","SWEPT_FACE",FACE,{"disambiguationData":[OSD([subQ0])]})]});}
            var Q1;
            {var subQ0=sQuery(id+"F14.wireOp",EDGE,"E3.top");Q1=makeQuery(id+"F41.boolean.opBoolean","MERGE",FACE,{"derivedFrom":[makeQuery(id+"F32.boolean.opBoolean","COPY",FACE,{"derivedFrom":makeQuery(id+"F32.opExtrude","CAP_FACE",FACE,{"disambiguationData":[OSD([subQ0])],"isStart":false})}),makeQuery(id+"F41.opExtrude","SWEPT_FACE",FACE,{"disambiguationData":[OSD([subQ0])]})]});}
            extrude(context, id + "F42", {"entities" : qUnion([Q0, Q1]), "operationType" : NewBodyOperationType.ADD, "depth" : 200 * mm, "offsetDistance" : 25 * mm});
        }
        {
            var Q0;
            {var subQ0=sQuery(id+"F10.wireOp",EDGE,"E2.left");var subQ1=sQuery(id+"F10.wireOp",EDGE,"E2.bottom");var subQ2=sQuery(id+"F4.wireOp",EDGE,"E1.bottom");Q0=makeQuery(id+"F41.boolean.opBoolean","MERGE",FACE,{"derivedFrom":[makeQuery(id+"F12.boolean.opBoolean","MERGE",FACE,{"derivedFrom":[makeQuery(id+"F11.boolean.opBoolean","SPLIT",FACE,{"disambiguationData":[TD([makeQuery(id+"F11.opExtrude","SWEPT_FACE",FACE,{"disambiguationData":[OSD([subQ0])]})])],"derivedFrom":makeQuery(id+"F6.boolean.opBoolean","COPY",FACE,{"derivedFrom":makeQuery(id+"F6.opExtrude","CAP_FACE",FACE,{"disambiguationData":[OSD([subQ2])],"isStart":false})})}),makeQuery(id+"F12.opExtrude","SWEPT_FACE",FACE,{"disambiguationData":[OSD([subQ2,subQ1,subQ0])]})]}),makeQuery(id+"F41.opExtrude","SWEPT_FACE",FACE,{"disambiguationData":[OSD([subQ2,subQ1,subQ0])]})]});}
            var Q1;
            {var subQ0=sQuery(id+"F10.wireOp",EDGE,"E2.right");var subQ1=sQuery(id+"F10.wireOp",EDGE,"E2.bottom");var subQ2=sQuery(id+"F4.wireOp",EDGE,"E1.bottom");Q1=makeQuery(id+"F41.boolean.opBoolean","MERGE",FACE,{"derivedFrom":[makeQuery(id+"F13.boolean.opBoolean","MERGE",FACE,{"derivedFrom":[makeQuery(id+"F11.boolean.opBoolean","SPLIT",FACE,{"disambiguationData":[TD([makeQuery(id+"F11.opExtrude","SWEPT_FACE",FACE,{"disambiguationData":[OSD([subQ0])]})])],"derivedFrom":makeQuery(id+"F6.boolean.opBoolean","COPY",FACE,{"derivedFrom":makeQuery(id+"F6.opExtrude","CAP_FACE",FACE,{"disambiguationData":[OSD([subQ2])],"isStart":false})})}),makeQuery(id+"F13.opExtrude","SWEPT_FACE",FACE,{"disambiguationData":[OSD([subQ2,subQ1,subQ0])]})]}),makeQuery(id+"F41.opExtrude","SWEPT_FACE",FACE,{"disambiguationData":[OSD([subQ2,subQ1,subQ0])]})]});}
            extrude(context, id + "F43", {"entities" : qUnion([Q0, Q1]), "operationType" : NewBodyOperationType.ADD, "depth" : 200 * mm, "offsetDistance" : 25 * mm});
        }
        {
            var Q0;
            Q0=makeQuery(id+"F3.opExtrude","CAP_FACE",FACE,{"disambiguationData":[OSD([sQuery(id+"F0.wireOp",EDGE,"E0.bottom"),sQuery(id+"F0.wireOp",EDGE,"E0.left")])],"isStart":false});
            var Q1;
            {var subQ0=sQuery(id+"F14.wireOp",EDGE,"E3.bottom");Q1=makeQuery(id+"F41.boolean.opBoolean","MERGE",FACE,{"derivedFrom":[makeQuery(id+"F31.opExtrude","CAP_FACE",FACE,{"disambiguationData":[OSD([subQ0])],"isStart":false}),makeQuery(id+"F41.opExtrude","SWEPT_FACE",FACE,{"disambiguationData":[OSD([subQ0])]})]});}
            var Q2;
            {var subQ0=sQuery(id+"F15.wireOp",EDGE,"E5.bottom");Q2=makeQuery(id+"F41.boolean.opBoolean","MERGE",FACE,{"derivedFrom":[makeQuery(id+"F37.boolean.opBoolean","COPY",FACE,{"derivedFrom":makeQuery(id+"F37.opExtrude","CAP_FACE",FACE,{"disambiguationData":[OSD([subQ0])],"isStart":false})}),makeQuery(id+"F41.opExtrude","SWEPT_FACE",FACE,{"disambiguationData":[OSD([subQ0])]})]});}
            extrude(context, id + "F44", {"entities" : qUnion([Q0, Q1, Q2]), "operationType" : NewBodyOperationType.REMOVE, "oppositeDirection" : true, "depth" : 200 * mm, "offsetDistance" : 25 * mm});
        }
        {
            var Q0;
            {var subQ0=sQuery(id+"F15.wireOp",EDGE,"E6.top");Q0=makeQuery(id+"F41.boolean.opBoolean","MERGE",FACE,{"derivedFrom":[makeQuery(id+"F40.boolean.opBoolean","COPY",FACE,{"derivedFrom":makeQuery(id+"F40.opExtrude","CAP_FACE",FACE,{"disambiguationData":[OSD([subQ0])],"isStart":false})}),makeQuery(id+"F41.opExtrude","SWEPT_FACE",FACE,{"disambiguationData":[OSD([subQ0])]})]});}
            var Q1;
            {var subQ0=sQuery(id+"F14.wireOp",EDGE,"E4.top");Q1=makeQuery(id+"F41.boolean.opBoolean","MERGE",FACE,{"derivedFrom":[makeQuery(id+"F33.opExtrude","CAP_FACE",FACE,{"disambiguationData":[OSD([subQ0])],"isStart":false}),makeQuery(id+"F41.opExtrude","SWEPT_FACE",FACE,{"disambiguationData":[OSD([subQ0])]})]});}
            extrude(context, id + "F45", {"entities" : qUnion([Q0, Q1]), "operationType" : NewBodyOperationType.ADD, "depth" : 70 * mm, "offsetDistance" : 25 * mm});
        }
        {
            var Q0;
            {var subQ0=sQuery(id+"F15.wireOp",EDGE,"E6.bottom");Q0=makeQuery(id+"F41.boolean.opBoolean","MERGE",FACE,{"derivedFrom":[makeQuery(id+"F39.opExtrude","CAP_FACE",FACE,{"disambiguationData":[OSD([subQ0])],"isStart":false}),makeQuery(id+"F41.opExtrude","SWEPT_FACE",FACE,{"disambiguationData":[OSD([subQ0])]})]});}
            var Q1;
            {var subQ0=sQuery(id+"F14.wireOp",EDGE,"E4.bottom");Q1=makeQuery(id+"F41.boolean.opBoolean","MERGE",FACE,{"derivedFrom":[makeQuery(id+"F34.boolean.opBoolean","COPY",FACE,{"derivedFrom":makeQuery(id+"F34.opExtrude","CAP_FACE",FACE,{"disambiguationData":[OSD([subQ0])],"isStart":false})}),makeQuery(id+"F41.opExtrude","SWEPT_FACE",FACE,{"disambiguationData":[OSD([subQ0])]})]});}
            extrude(context, id + "F46", {"entities" : qUnion([Q0, Q1]), "operationType" : NewBodyOperationType.REMOVE, "oppositeDirection" : true, "depth" : 70 * mm, "offsetDistance" : 25 * mm});
        }
        {
            var Q0;
            Q0=makeQuery(id+"F44.boolean.opBoolean","COPY",FACE,{"derivedFrom":makeQuery(id+"F44.opExtrude","CAP_FACE",FACE,{"disambiguationData":[OSD([sQuery(id+"F15.wireOp",EDGE,"E5.bottom")])],"isStart":false})});
            var Q1;
            Q1=makeQuery(id+"F44.boolean.opBoolean","COPY",FACE,{"derivedFrom":makeQuery(id+"F44.opExtrude","CAP_FACE",FACE,{"disambiguationData":[OSD([sQuery(id+"F14.wireOp",EDGE,"E3.bottom")])],"isStart":false})});
            extrude(context, id + "F47", {"entities" : qUnion([Q0, Q1]), "operationType" : NewBodyOperationType.ADD, "depth" : 70 * mm, "offsetDistance" : 25 * mm});
        }
        {
            var Q0;
            Q0=makeQuery(id+"F42.opExtrude","CAP_FACE",FACE,{"disambiguationData":[OSD([sQuery(id+"F15.wireOp",EDGE,"E5.top")])],"isStart":false});
            var Q1;
            Q1=makeQuery(id+"F42.opExtrude","CAP_FACE",FACE,{"disambiguationData":[OSD([sQuery(id+"F14.wireOp",EDGE,"E3.top")])],"isStart":false});
            extrude(context, id + "F48", {"entities" : qUnion([Q0, Q1]), "operationType" : NewBodyOperationType.REMOVE, "oppositeDirection" : true, "depth" : 70 * mm, "offsetDistance" : 25 * mm});
        }
        {
            var Q0;
            {var subQ0=sQuery(id+"F0.wireOp",EDGE,"E0.left");var subQ1=sQuery(id+"F0.wireOp",EDGE,"E0.bottom");Q0=makeQuery(id+"F3.boolean.opBoolean","MERGE",FACE,{"derivedFrom":[makeQuery(id+"F2.opExtrude","CAP_FACE",FACE,{"disambiguationData":[OSD([subQ0])],"isStart":false}),makeQuery(id+"F3.opExtrude","SWEPT_FACE",FACE,{"disambiguationData":[OSD([subQ1,subQ0]),TDD([makeQuery(id+"F2.opExtrude","CAP_EDGE",EDGE,{"disambiguationData":[OSD([subQ1,subQ0])],"isStart":false})])]})]});}
            extrude(context, id + "F49", {"entities" : qUnion([Q0]), "operationType" : NewBodyOperationType.ADD, "depth" : 100 * mm, "offsetDistance" : 25 * mm});
        }
        {
            var Q0;
            {var subQ0=sQuery(id+"F15.wireOp",EDGE,"E5.left");var subQ1=sQuery(id+"F15.wireOp",EDGE,"E5.top");var subQ2=sQuery(id+"F10.wireOp",EDGE,"E2.right");var subQ3=sQuery(id+"F15.wireOp",EDGE,"E6.left");var subQ4=sQuery(id+"F15.wireOp",EDGE,"E6.bottom");Q0=makeQuery(id+"F48.boolean.opBoolean","MERGE",FACE,{"derivedFrom":[makeQuery(id+"F46.boolean.opBoolean","MERGE",FACE,{"derivedFrom":[makeQuery(id+"F41.boolean.opBoolean","MERGE",FACE,{"derivedFrom":[makeQuery(id+"F35.boolean.opBoolean","MERGE",FACE,{"derivedFrom":[makeQuery(id+"F18.boolean.opBoolean","MERGE",FACE,{"derivedFrom":[makeQuery(id+"F16.boolean.opBoolean","SPLIT",FACE,{"disambiguationData":[TD([makeQuery(id+"F16.opExtrude","SWEPT_FACE",FACE,{"disambiguationData":[OSD([subQ1])]})])],"derivedFrom":makeQuery(id+"F13.boolean.opBoolean","COPY",FACE,{"derivedFrom":makeQuery(id+"F13.opExtrude","CAP_FACE",FACE,{"disambiguationData":[OSD([subQ2])],"isStart":false})})}),makeQuery(id+"F18.opExtrude","SWEPT_FACE",FACE,{"disambiguationData":[OSD([subQ2,subQ4,subQ3])]})]}),makeQuery(id+"F35.opExtrude","SWEPT_FACE",FACE,{"disambiguationData":[OSD([subQ2,subQ1,subQ0])]})]}),makeQuery(id+"F41.opExtrude","SWEPT_FACE",FACE,{"disambiguationData":[OSD([subQ2,subQ1,subQ0,subQ4,subQ3])]})]}),makeQuery(id+"F46.opExtrude","SWEPT_FACE",FACE,{"disambiguationData":[OSD([subQ2,subQ4,subQ3])]})]}),makeQuery(id+"F48.opExtrude","SWEPT_FACE",FACE,{"disambiguationData":[OSD([subQ2,subQ1,subQ0])]})]});}
            var Q1;
            {var subQ0=sQuery(id+"F15.wireOp",EDGE,"E6.left");var subQ1=sQuery(id+"F15.wireOp",EDGE,"E6.top");var subQ2=sQuery(id+"F10.wireOp",EDGE,"E2.right");var subQ3=sQuery(id+"F4.wireOp",EDGE,"E1.top");Q1=makeQuery(id+"F41.boolean.opBoolean","MERGE",FACE,{"derivedFrom":[makeQuery(id+"F40.boolean.opBoolean","MERGE",FACE,{"derivedFrom":[makeQuery(id+"F38.boolean.opBoolean","MERGE",FACE,{"derivedFrom":[makeQuery(id+"F16.boolean.opBoolean","SPLIT",FACE,{"disambiguationData":[TD([makeQuery(id+"F8.boolean.opBoolean","COPY",FACE,{"derivedFrom":makeQuery(id+"F8.opExtrude","CAP_FACE",FACE,{"disambiguationData":[OSD([subQ3])],"isStart":false})})])],"derivedFrom":makeQuery(id+"F13.boolean.opBoolean","COPY",FACE,{"derivedFrom":makeQuery(id+"F13.opExtrude","CAP_FACE",FACE,{"disambiguationData":[OSD([subQ2])],"isStart":false})})}),makeQuery(id+"F38.opExtrude","SWEPT_FACE",FACE,{"disambiguationData":[OSD([subQ2,subQ1,subQ0])]})]}),makeQuery(id+"F40.opExtrude","SWEPT_FACE",FACE,{"disambiguationData":[OSD([subQ2,subQ1,subQ0])]})]}),makeQuery(id+"F41.opExtrude","SWEPT_FACE",FACE,{"disambiguationData":[OSD([subQ2,subQ1,subQ0])]})]});}
            var Q2;
            {var subQ0=sQuery(id+"F15.wireOp",EDGE,"E5.left");var subQ1=sQuery(id+"F15.wireOp",EDGE,"E5.bottom");var subQ2=sQuery(id+"F10.wireOp",EDGE,"E2.right");var subQ6=sQuery(id+"F4.wireOp",EDGE,"E1.bottom");Q2=makeQuery(id+"F44.boolean.opBoolean","MERGE",FACE,{"derivedFrom":[makeQuery(id+"F41.boolean.opBoolean","MERGE",FACE,{"derivedFrom":[makeQuery(id+"F37.boolean.opBoolean","MERGE",FACE,{"derivedFrom":[makeQuery(id+"F16.boolean.opBoolean","SPLIT",FACE,{"disambiguationData":[TD([makeQuery(id+"F6.boolean.opBoolean","COPY",FACE,{"derivedFrom":makeQuery(id+"F6.opExtrude","CAP_FACE",FACE,{"disambiguationData":[OSD([subQ6])],"isStart":false})})])],"derivedFrom":makeQuery(id+"F13.boolean.opBoolean","COPY",FACE,{"derivedFrom":makeQuery(id+"F13.opExtrude","CAP_FACE",FACE,{"disambiguationData":[OSD([subQ2])],"isStart":false})})}),makeQuery(id+"F37.opExtrude","SWEPT_FACE",FACE,{"disambiguationData":[OSD([subQ2,subQ1,subQ0])]})]}),makeQuery(id+"F41.opExtrude","SWEPT_FACE",FACE,{"disambiguationData":[OSD([subQ2,subQ1,subQ0])]})]}),makeQuery(id+"F44.opExtrude","SWEPT_FACE",FACE,{"disambiguationData":[OSD([subQ2,subQ1,subQ0])]})]});}
            extrude(context, id + "F50", {"entities" : qUnion([Q0, Q1, Q2]), "operationType" : NewBodyOperationType.ADD, "depth" : 50 * mm, "offsetDistance" : 25 * mm});
        }
        {
            var Q0;
            {var subQ0=sQuery(id+"F15.wireOp",EDGE,"E5.right");var subQ1=sQuery(id+"F15.wireOp",EDGE,"E5.bottom");var subQ2=sQuery(id+"F4.wireOp",EDGE,"E1.right");var subQ3=sQuery(id+"F4.wireOp",EDGE,"E1.top");var subQ4=sQuery(id+"F4.wireOp",EDGE,"E1.bottom");Q0=makeQuery(id+"F44.boolean.opBoolean","MERGE",FACE,{"derivedFrom":[makeQuery(id+"F41.boolean.opBoolean","MERGE",FACE,{"derivedFrom":[makeQuery(id+"F37.boolean.opBoolean","MERGE",FACE,{"derivedFrom":[makeQuery(id+"F16.boolean.opBoolean","SPLIT",FACE,{"disambiguationData":[TD([makeQuery(id+"F6.boolean.opBoolean","COPY",FACE,{"derivedFrom":makeQuery(id+"F6.opExtrude","CAP_FACE",FACE,{"disambiguationData":[OSD([subQ4])],"isStart":false})})])],"derivedFrom":makeQuery(id+"F8.boolean.opBoolean","MERGE",FACE,{"derivedFrom":[makeQuery(id+"F7.opExtrude","CAP_FACE",FACE,{"disambiguationData":[OSD([subQ4,subQ2])],"isStart":false}),makeQuery(id+"F8.opExtrude","SWEPT_FACE",FACE,{"disambiguationData":[OSD([subQ3,subQ2])]})]})}),makeQuery(id+"F37.opExtrude","SWEPT_FACE",FACE,{"disambiguationData":[OSD([subQ4,subQ3,subQ2,subQ1,subQ0])]})]}),makeQuery(id+"F41.opExtrude","SWEPT_FACE",FACE,{"disambiguationData":[OSD([subQ4,subQ3,subQ2,subQ1,subQ0])]})]}),makeQuery(id+"F44.opExtrude","SWEPT_FACE",FACE,{"disambiguationData":[OSD([subQ4,subQ3,subQ2,subQ1,subQ0])]})]});}
            var Q1;
            {var subQ0=sQuery(id+"F15.wireOp",EDGE,"E5.right");var subQ1=sQuery(id+"F15.wireOp",EDGE,"E5.top");var subQ2=sQuery(id+"F4.wireOp",EDGE,"E1.right");var subQ3=sQuery(id+"F4.wireOp",EDGE,"E1.top");var subQ4=sQuery(id+"F4.wireOp",EDGE,"E1.bottom");var subQ5=sQuery(id+"F15.wireOp",EDGE,"E6.right");var subQ6=sQuery(id+"F15.wireOp",EDGE,"E6.bottom");Q1=makeQuery(id+"F48.boolean.opBoolean","MERGE",FACE,{"derivedFrom":[makeQuery(id+"F46.boolean.opBoolean","MERGE",FACE,{"derivedFrom":[makeQuery(id+"F41.boolean.opBoolean","MERGE",FACE,{"derivedFrom":[makeQuery(id+"F35.boolean.opBoolean","MERGE",FACE,{"derivedFrom":[makeQuery(id+"F18.boolean.opBoolean","MERGE",FACE,{"derivedFrom":[makeQuery(id+"F16.boolean.opBoolean","SPLIT",FACE,{"disambiguationData":[TD([makeQuery(id+"F16.opExtrude","SWEPT_FACE",FACE,{"disambiguationData":[OSD([subQ1])]})])],"derivedFrom":makeQuery(id+"F8.boolean.opBoolean","MERGE",FACE,{"derivedFrom":[makeQuery(id+"F7.opExtrude","CAP_FACE",FACE,{"disambiguationData":[OSD([subQ4,subQ2])],"isStart":false}),makeQuery(id+"F8.opExtrude","SWEPT_FACE",FACE,{"disambiguationData":[OSD([subQ3,subQ2])]})]})}),makeQuery(id+"F18.opExtrude","SWEPT_FACE",FACE,{"disambiguationData":[OSD([subQ4,subQ3,subQ2,subQ6,subQ5])]})]}),makeQuery(id+"F35.opExtrude","SWEPT_FACE",FACE,{"disambiguationData":[OSD([subQ4,subQ3,subQ2,subQ1,subQ0])]})]}),makeQuery(id+"F41.opExtrude","SWEPT_FACE",FACE,{"disambiguationData":[OSD([subQ4,subQ3,subQ2,subQ1,subQ0,subQ6,subQ5])]})]}),makeQuery(id+"F46.opExtrude","SWEPT_FACE",FACE,{"disambiguationData":[OSD([subQ4,subQ3,subQ2,subQ6,subQ5])]})]}),makeQuery(id+"F48.opExtrude","SWEPT_FACE",FACE,{"disambiguationData":[OSD([subQ4,subQ3,subQ2,subQ1,subQ0])]})]});}
            var Q2;
            {var subQ0=sQuery(id+"F15.wireOp",EDGE,"E6.right");var subQ1=sQuery(id+"F15.wireOp",EDGE,"E6.top");var subQ2=sQuery(id+"F4.wireOp",EDGE,"E1.right");var subQ3=sQuery(id+"F4.wireOp",EDGE,"E1.top");var subQ4=sQuery(id+"F4.wireOp",EDGE,"E1.bottom");Q2=makeQuery(id+"F41.boolean.opBoolean","MERGE",FACE,{"derivedFrom":[makeQuery(id+"F40.boolean.opBoolean","MERGE",FACE,{"derivedFrom":[makeQuery(id+"F38.boolean.opBoolean","MERGE",FACE,{"derivedFrom":[makeQuery(id+"F16.boolean.opBoolean","SPLIT",FACE,{"disambiguationData":[TD([makeQuery(id+"F8.boolean.opBoolean","COPY",FACE,{"derivedFrom":makeQuery(id+"F8.opExtrude","CAP_FACE",FACE,{"disambiguationData":[OSD([subQ3])],"isStart":false})})])],"derivedFrom":makeQuery(id+"F8.boolean.opBoolean","MERGE",FACE,{"derivedFrom":[makeQuery(id+"F7.opExtrude","CAP_FACE",FACE,{"disambiguationData":[OSD([subQ4,subQ2])],"isStart":false}),makeQuery(id+"F8.opExtrude","SWEPT_FACE",FACE,{"disambiguationData":[OSD([subQ3,subQ2])]})]})}),makeQuery(id+"F38.opExtrude","SWEPT_FACE",FACE,{"disambiguationData":[OSD([subQ4,subQ3,subQ2,subQ1,subQ0])]})]}),makeQuery(id+"F40.opExtrude","SWEPT_FACE",FACE,{"disambiguationData":[OSD([subQ4,subQ3,subQ2,subQ1,subQ0])]})]}),makeQuery(id+"F41.opExtrude","SWEPT_FACE",FACE,{"disambiguationData":[OSD([subQ4,subQ3,subQ2,subQ1,subQ0])]})]});}
            extrude(context, id + "F51", {"entities" : qUnion([Q0, Q1, Q2]), "operationType" : NewBodyOperationType.REMOVE, "oppositeDirection" : true, "depth" : 100 * mm, "offsetDistance" : 25 * mm});
        }
        {
            var Q0;
            {var subQ0=sQuery(id+"F14.wireOp",EDGE,"E3.right");var subQ1=sQuery(id+"F14.wireOp",EDGE,"E3.top");var subQ2=sQuery(id+"F10.wireOp",EDGE,"E2.left");var subQ3=sQuery(id+"F14.wireOp",EDGE,"E4.right");var subQ4=sQuery(id+"F14.wireOp",EDGE,"E4.bottom");Q0=makeQuery(id+"F48.boolean.opBoolean","MERGE",FACE,{"derivedFrom":[makeQuery(id+"F46.boolean.opBoolean","MERGE",FACE,{"derivedFrom":[makeQuery(id+"F41.boolean.opBoolean","MERGE",FACE,{"derivedFrom":[makeQuery(id+"F34.boolean.opBoolean","MERGE",FACE,{"derivedFrom":[makeQuery(id+"F32.boolean.opBoolean","MERGE",FACE,{"derivedFrom":[makeQuery(id+"F26.boolean.opBoolean","MERGE",FACE,{"derivedFrom":[makeQuery(id+"F24.boolean.opBoolean","MERGE",FACE,{"derivedFrom":[makeQuery(id+"F18.boolean.opBoolean","MERGE",FACE,{"derivedFrom":[makeQuery(id+"F16.boolean.opBoolean","SPLIT",FACE,{"disambiguationData":[TD([makeQuery(id+"F16.opExtrude","SWEPT_FACE",FACE,{"disambiguationData":[OSD([subQ1])]})])],"derivedFrom":makeQuery(id+"F12.boolean.opBoolean","COPY",FACE,{"derivedFrom":makeQuery(id+"F12.opExtrude","CAP_FACE",FACE,{"disambiguationData":[OSD([subQ2])],"isStart":false})})}),makeQuery(id+"F18.opExtrude","SWEPT_FACE",FACE,{"disambiguationData":[OSD([subQ2,subQ4,subQ3])]})]}),makeQuery(id+"F24.opExtrude","SWEPT_FACE",FACE,{"disambiguationData":[OSD([subQ2,subQ1,subQ0])]})]}),makeQuery(id+"F26.opExtrude","SWEPT_FACE",FACE,{"disambiguationData":[OSD([subQ2,subQ1,subQ0])]})]}),makeQuery(id+"F32.opExtrude","SWEPT_FACE",FACE,{"disambiguationData":[OSD([subQ2,subQ1,subQ0])]})]}),makeQuery(id+"F34.opExtrude","SWEPT_FACE",FACE,{"disambiguationData":[OSD([subQ2,subQ4,subQ3])]})]}),makeQuery(id+"F41.opExtrude","SWEPT_FACE",FACE,{"disambiguationData":[OSD([subQ2,subQ1,subQ0,subQ4,subQ3])]})]}),makeQuery(id+"F46.opExtrude","SWEPT_FACE",FACE,{"disambiguationData":[OSD([subQ2,subQ4,subQ3])]})]}),makeQuery(id+"F48.opExtrude","SWEPT_FACE",FACE,{"disambiguationData":[OSD([subQ2,subQ1,subQ0])]})]});}
            var Q1;
            {var subQ0=sQuery(id+"F14.wireOp",EDGE,"E3.right");var subQ1=sQuery(id+"F14.wireOp",EDGE,"E3.bottom");var subQ2=sQuery(id+"F10.wireOp",EDGE,"E2.left");var subQ6=sQuery(id+"F4.wireOp",EDGE,"E1.bottom");Q1=makeQuery(id+"F44.boolean.opBoolean","MERGE",FACE,{"derivedFrom":[makeQuery(id+"F41.boolean.opBoolean","MERGE",FACE,{"derivedFrom":[makeQuery(id+"F30.boolean.opBoolean","MERGE",FACE,{"derivedFrom":[makeQuery(id+"F20.boolean.opBoolean","MERGE",FACE,{"derivedFrom":[makeQuery(id+"F16.boolean.opBoolean","SPLIT",FACE,{"disambiguationData":[TD([makeQuery(id+"F6.boolean.opBoolean","COPY",FACE,{"derivedFrom":makeQuery(id+"F6.opExtrude","CAP_FACE",FACE,{"disambiguationData":[OSD([subQ6])],"isStart":false})})])],"derivedFrom":makeQuery(id+"F12.boolean.opBoolean","COPY",FACE,{"derivedFrom":makeQuery(id+"F12.opExtrude","CAP_FACE",FACE,{"disambiguationData":[OSD([subQ2])],"isStart":false})})}),makeQuery(id+"F20.opExtrude","SWEPT_FACE",FACE,{"disambiguationData":[OSD([subQ2,subQ1,subQ0])]})]}),makeQuery(id+"F30.opExtrude","SWEPT_FACE",FACE,{"disambiguationData":[OSD([subQ2,subQ1,subQ0])]})]}),makeQuery(id+"F41.opExtrude","SWEPT_FACE",FACE,{"disambiguationData":[OSD([subQ2,subQ1,subQ0])]})]}),makeQuery(id+"F44.opExtrude","SWEPT_FACE",FACE,{"disambiguationData":[OSD([subQ2,subQ1,subQ0])]})]});}
            var Q2;
            {var subQ0=sQuery(id+"F14.wireOp",EDGE,"E4.right");var subQ1=sQuery(id+"F14.wireOp",EDGE,"E4.top");var subQ2=sQuery(id+"F10.wireOp",EDGE,"E2.left");var subQ3=sQuery(id+"F4.wireOp",EDGE,"E1.top");Q2=makeQuery(id+"F41.boolean.opBoolean","MERGE",FACE,{"derivedFrom":[makeQuery(id+"F28.boolean.opBoolean","MERGE",FACE,{"derivedFrom":[makeQuery(id+"F22.boolean.opBoolean","MERGE",FACE,{"derivedFrom":[makeQuery(id+"F16.boolean.opBoolean","SPLIT",FACE,{"disambiguationData":[TD([makeQuery(id+"F8.boolean.opBoolean","COPY",FACE,{"derivedFrom":makeQuery(id+"F8.opExtrude","CAP_FACE",FACE,{"disambiguationData":[OSD([subQ3])],"isStart":false})})])],"derivedFrom":makeQuery(id+"F12.boolean.opBoolean","COPY",FACE,{"derivedFrom":makeQuery(id+"F12.opExtrude","CAP_FACE",FACE,{"disambiguationData":[OSD([subQ2])],"isStart":false})})}),makeQuery(id+"F22.opExtrude","SWEPT_FACE",FACE,{"disambiguationData":[OSD([subQ2,subQ1,subQ0])]})]}),makeQuery(id+"F28.opExtrude","SWEPT_FACE",FACE,{"disambiguationData":[OSD([subQ2,subQ1,subQ0])]})]}),makeQuery(id+"F41.opExtrude","SWEPT_FACE",FACE,{"disambiguationData":[OSD([subQ2,subQ1,subQ0])]})]});}
            extrude(context, id + "F52", {"entities" : qUnion([Q0, Q1, Q2]), "operationType" : NewBodyOperationType.REMOVE, "oppositeDirection" : true, "depth" : 50 * mm, "offsetDistance" : 25 * mm});
        }
        {
            var Q0;
            {var subQ0=sQuery(id+"F15.wireOp",EDGE,"E5.left");var subQ1=sQuery(id+"F15.wireOp",EDGE,"E5.top");var subQ2=sQuery(id+"F10.wireOp",EDGE,"E2.right");var subQ3=makeQuery(id+"F16.opExtrude","CAP_VERTEX",VERTEX,{"disambiguationData":[OSD([subQ2,subQ1,subQ0])],"isStart":false});var subQ4=sQuery(id+"F15.wireOp",EDGE,"E6.left");var subQ5=sQuery(id+"F15.wireOp",EDGE,"E6.bottom");var subQ6=makeQuery(id+"F16.opExtrude","CAP_VERTEX",VERTEX,{"disambiguationData":[OSD([subQ2,subQ5,subQ4])],"isStart":false});var subQ7=sQuery(id+"F15.wireOp",EDGE,"E5.bottom");var subQ8=makeQuery(id+"F16.opExtrude","CAP_FACE",FACE,{"disambiguationData":[OSD([subQ7,subQ1,subQ0,sQuery(id+"F15.wireOp",EDGE,"E5.right")])],"isStart":false});var subQ9=sQuery(id+"F14.wireOp",EDGE,"E4.top");var subQ10=sQuery(id+"F14.wireOp",EDGE,"E4.bottom");var subQ11=makeQuery(id+"F16.opExtrude","CAP_FACE",FACE,{"disambiguationData":[OSD([subQ10,subQ9,sQuery(id+"F14.wireOp",EDGE,"E4.left"),sQuery(id+"F14.wireOp",EDGE,"E4.right")])],"isStart":false});var subQ12=sQuery(id+"F14.wireOp",EDGE,"E3.top");var subQ13=sQuery(id+"F14.wireOp",EDGE,"E3.bottom");var subQ14=makeQuery(id+"F16.opExtrude","CAP_FACE",FACE,{"disambiguationData":[OSD([subQ13,subQ12,sQuery(id+"F14.wireOp",EDGE,"E3.left"),sQuery(id+"F14.wireOp",EDGE,"E3.right")])],"isStart":false});var subQ16=sQuery(id+"F10.wireOp",EDGE,"E2.left");var subQ17=sQuery(id+"F10.wireOp",EDGE,"E2.top");var subQ18=sQuery(id+"F10.wireOp",EDGE,"E2.bottom");var subQ19=makeQuery(id+"F11.opExtrude","CAP_FACE",FACE,{"disambiguationData":[OSD([subQ18,subQ17,subQ16,subQ2])],"isStart":false});var subQ20=sQuery(id+"F0.wireOp",EDGE,"E0.left");var subQ21=makeQuery(id+"F1.opExtrude","CAP_EDGE",EDGE,{"disambiguationData":[OSD([subQ20])],"isStart":false});var subQ22=makeQuery(id+"F2.opExtrude","SWEPT_FACE",FACE,{"disambiguationData":[OSD([subQ20]),TDD([subQ21])]});var subQ23=sQuery(id+"F4.wireOp",EDGE,"E1.left");var subQ24=sQuery(id+"F4.wireOp",EDGE,"E1.top");var subQ25=sQuery(id+"F4.wireOp",EDGE,"E1.bottom");var subQ26=makeQuery(id+"F9.opExtrude","SWEPT_FACE",FACE,{"disambiguationData":[OSD([subQ25,subQ24,subQ23]),TDD([makeQuery(id+"F8.boolean.opBoolean","MERGE",EDGE,{"derivedFrom":[makeQuery(id+"F6.boolean.opBoolean","MERGE",EDGE,{"derivedFrom":[makeQuery(id+"F5.boolean.opBoolean","COPY",EDGE,{"derivedFrom":makeQuery(id+"F5.opExtrude","CAP_EDGE",EDGE,{"disambiguationData":[OSD([subQ23])],"isStart":true})}),makeQuery(id+"F6.opExtrude","SWEPT_EDGE",EDGE,{"disambiguationData":[OSD([subQ25,subQ23]),TDD([makeQuery(id+"F5.boolean.opBoolean","COPY",VERTEX,{"derivedFrom":makeQuery(id+"F5.opExtrude","CAP_VERTEX",VERTEX,{"disambiguationData":[OSD([subQ25,subQ23])],"isStart":true})})])]})]}),makeQuery(id+"F8.opExtrude","SWEPT_EDGE",EDGE,{"disambiguationData":[OSD([subQ24,subQ23]),TDD([makeQuery(id+"F5.boolean.opBoolean","COPY",VERTEX,{"derivedFrom":makeQuery(id+"F5.opExtrude","CAP_VERTEX",VERTEX,{"disambiguationData":[OSD([subQ24,subQ23])],"isStart":true})})])]})]})])]});var subQ27=sQuery(id+"F0.wireOp",EDGE,"E0.bottom");var subQ28=makeQuery(id+"F1.opExtrude","CAP_FACE",FACE,{"disambiguationData":[OSD([subQ27,sQuery(id+"F0.wireOp",EDGE,"E0.top"),subQ20,sQuery(id+"F0.wireOp",EDGE,"E0.right")])],"isStart":false});var subQ29=sQuery(id+"F4.wireOp",EDGE,"E1.right");var subQ30=makeQuery(id+"F7.opExtrude","SWEPT_FACE",FACE,{"disambiguationData":[OSD([subQ25,subQ29]),TDD([makeQuery(id+"F6.boolean.opBoolean","MERGE",EDGE,{"derivedFrom":[makeQuery(id+"F5.boolean.opBoolean","COPY",EDGE,{"derivedFrom":makeQuery(id+"F5.opExtrude","CAP_EDGE",EDGE,{"disambiguationData":[OSD([subQ29])],"isStart":true})}),makeQuery(id+"F6.opExtrude","SWEPT_EDGE",EDGE,{"disambiguationData":[OSD([subQ25,subQ29]),TDD([makeQuery(id+"F5.boolean.opBoolean","COPY",VERTEX,{"derivedFrom":makeQuery(id+"F5.opExtrude","CAP_VERTEX",VERTEX,{"disambiguationData":[OSD([subQ25,subQ29])],"isStart":true})})])]})]})])]});var subQ31=makeQuery(id+"F1.opExtrude","CAP_VERTEX",VERTEX,{"disambiguationData":[OSD([subQ27,subQ20])],"isStart":false});var subQ32=makeQuery(id+"F3.opExtrude","SWEPT_FACE",FACE,{"disambiguationData":[OSD([subQ27,subQ20]),TDD([makeQuery(id+"F2.boolean.opBoolean","MERGE",EDGE,{"derivedFrom":[makeQuery(id+"F1.opExtrude","CAP_EDGE",EDGE,{"disambiguationData":[OSD([subQ27])],"isStart":false}),makeQuery(id+"F2.opExtrude","SWEPT_EDGE",EDGE,{"disambiguationData":[OSD([subQ27,subQ20]),TDD([subQ31])]})]})])]});var subQ33=sQuery(id+"F15.wireOp",EDGE,"E6.top");var subQ34=makeQuery(id+"F16.opExtrude","CAP_FACE",FACE,{"disambiguationData":[OSD([subQ5,subQ33,subQ4,sQuery(id+"F15.wireOp",EDGE,"E6.right")])],"isStart":false});var subQ35=makeQuery(id+"F13.boolean.opBoolean","COPY",EDGE,{"derivedFrom":makeQuery(id+"F13.opExtrude","CAP_EDGE",EDGE,{"disambiguationData":[OSD([subQ2]),TDD([makeQuery(id+"F11.opExtrude","CAP_EDGE",EDGE,{"disambiguationData":[OSD([subQ2])],"isStart":false})])],"isStart":false})});var subQ36=makeQuery(id+"F16.opExtrude","CAP_VERTEX",VERTEX,{"disambiguationData":[OSD([subQ2,subQ7,subQ0])],"isStart":false});var subQ37=makeQuery(id+"F6.boolean.opBoolean","COPY",FACE,{"derivedFrom":makeQuery(id+"F6.opExtrude","CAP_FACE",FACE,{"disambiguationData":[OSD([subQ25])],"isStart":false})});var subQ38=makeQuery(id+"F17.opExtrude","CAP_VERTEX",VERTEX,{"disambiguationData":[OSD([subQ2,subQ33,subQ4]),TDD([makeQuery(id+"F16.opExtrude","CAP_VERTEX",VERTEX,{"disambiguationData":[OSD([subQ2,subQ33,subQ4])],"isStart":false})])],"isStart":false});var subQ39=makeQuery(id+"F20.boolean.opBoolean","COPY",EDGE,{"derivedFrom":makeQuery(id+"F20.opExtrude","CAP_EDGE",EDGE,{"disambiguationData":[OSD([subQ13]),TDD([makeQuery(id+"F16.opExtrude","CAP_EDGE",EDGE,{"disambiguationData":[OSD([subQ13])],"isStart":false})])],"isStart":false})});var subQ40=makeQuery(id+"F23.opExtrude","CAP_EDGE",EDGE,{"disambiguationData":[OSD([subQ13]),TDD([subQ39])],"isStart":false});var subQ41=makeQuery(id+"F30.boolean.opBoolean","COPY",EDGE,{"derivedFrom":makeQuery(id+"F30.opExtrude","CAP_EDGE",EDGE,{"disambiguationData":[OSD([subQ13]),TDD([makeQuery(id+"F25.opExtrude","CAP_EDGE",EDGE,{"disambiguationData":[OSD([subQ13]),TDD([subQ40])],"isStart":false})])],"isStart":false})});var subQ42=makeQuery(id+"F16.opExtrude","CAP_EDGE",EDGE,{"disambiguationData":[OSD([subQ33])],"isStart":false});var subQ43=makeQuery(id+"F16.opExtrude","CAP_EDGE",EDGE,{"disambiguationData":[OSD([subQ9])],"isStart":false});var subQ44=makeQuery(id+"F22.boolean.opBoolean","COPY",EDGE,{"derivedFrom":makeQuery(id+"F22.opExtrude","CAP_EDGE",EDGE,{"disambiguationData":[OSD([subQ9]),TDD([makeQuery(id+"F17.opExtrude","CAP_EDGE",EDGE,{"disambiguationData":[OSD([subQ9]),TDD([subQ43])],"isStart":false})])],"isStart":false})});var subQ45=makeQuery(id+"F28.boolean.opBoolean","COPY",EDGE,{"derivedFrom":makeQuery(id+"F28.opExtrude","CAP_EDGE",EDGE,{"disambiguationData":[OSD([subQ9]),TDD([makeQuery(id+"F27.opExtrude","CAP_EDGE",EDGE,{"disambiguationData":[OSD([subQ9]),TDD([subQ44])],"isStart":false})])],"isStart":false})});var subQ46=makeQuery(id+"F6.boolean.opBoolean","COPY",EDGE,{"derivedFrom":makeQuery(id+"F6.opExtrude","CAP_EDGE",EDGE,{"disambiguationData":[OSD([subQ25]),TDD([makeQuery(id+"F5.boolean.opBoolean","COPY",EDGE,{"derivedFrom":makeQuery(id+"F5.opExtrude","CAP_EDGE",EDGE,{"disambiguationData":[OSD([subQ25])],"isStart":true})})])],"isStart":false})});var subQ47=makeQuery(id+"F35.boolean.opBoolean","COPY",EDGE,{"derivedFrom":makeQuery(id+"F35.opExtrude","CAP_EDGE",EDGE,{"disambiguationData":[OSD([subQ1]),TDD([makeQuery(id+"F16.opExtrude","CAP_EDGE",EDGE,{"disambiguationData":[OSD([subQ1])],"isStart":false})])],"isStart":false})});var subQ48=makeQuery(id+"F16.opExtrude","CAP_EDGE",EDGE,{"disambiguationData":[OSD([subQ12])],"isStart":false});var subQ49=makeQuery(id+"F26.boolean.opBoolean","COPY",EDGE,{"derivedFrom":makeQuery(id+"F26.opExtrude","CAP_EDGE",EDGE,{"disambiguationData":[OSD([subQ12]),TDD([makeQuery(id+"F24.boolean.opBoolean","COPY",EDGE,{"derivedFrom":makeQuery(id+"F24.opExtrude","CAP_EDGE",EDGE,{"disambiguationData":[OSD([subQ12]),TDD([makeQuery(id+"F19.opExtrude","CAP_EDGE",EDGE,{"disambiguationData":[OSD([subQ12]),TDD([subQ48])],"isStart":false})])],"isStart":false})})])],"isStart":false})});Q0=makeQuery(id+"F50.boolean.opBoolean","MERGE",FACE,{"derivedFrom":[makeQuery(id+"F49.boolean.opBoolean","MERGE",FACE,{"derivedFrom":[makeQuery(id+"F47.boolean.opBoolean","MERGE",FACE,{"derivedFrom":[makeQuery(id+"F45.boolean.opBoolean","MERGE",FACE,{"derivedFrom":[makeQuery(id+"F43.boolean.opBoolean","MERGE",FACE,{"derivedFrom":[makeQuery(id+"F42.boolean.opBoolean","MERGE",FACE,{"derivedFrom":[makeQuery(id+"F39.boolean.opBoolean","MERGE",FACE,{"derivedFrom":[makeQuery(id+"F36.boolean.opBoolean","MERGE",FACE,{"derivedFrom":[makeQuery(id+"F33.boolean.opBoolean","MERGE",FACE,{"derivedFrom":[makeQuery(id+"F31.boolean.opBoolean","MERGE",FACE,{"derivedFrom":[makeQuery(id+"F29.boolean.opBoolean","MERGE",FACE,{"derivedFrom":[makeQuery(id+"F27.boolean.opBoolean","MERGE",FACE,{"derivedFrom":[makeQuery(id+"F25.boolean.opBoolean","MERGE",FACE,{"derivedFrom":[makeQuery(id+"F23.boolean.opBoolean","MERGE",FACE,{"derivedFrom":[makeQuery(id+"F21.boolean.opBoolean","MERGE",FACE,{"derivedFrom":[makeQuery(id+"F19.boolean.opBoolean","MERGE",FACE,{"derivedFrom":[makeQuery(id+"F17.boolean.opBoolean","MERGE",FACE,{"derivedFrom":[makeQuery(id+"F16.boolean.opBoolean","MERGE",FACE,{"derivedFrom":[makeQuery(id+"F11.boolean.opBoolean","MERGE",FACE,{"derivedFrom":[makeQuery(id+"F9.boolean.opBoolean","MERGE",FACE,{"derivedFrom":[makeQuery(id+"F7.boolean.opBoolean","MERGE",FACE,{"derivedFrom":[makeQuery(id+"F3.boolean.opBoolean","MERGE",FACE,{"derivedFrom":[makeQuery(id+"F2.boolean.opBoolean","MERGE",FACE,{"derivedFrom":[subQ28,subQ22]}),subQ32]}),subQ30]}),subQ26]}),subQ19]}),subQ14,subQ11,subQ8,subQ34]}),makeQuery(id+"F17.opExtrude","SWEPT_FACE",FACE,{"disambiguationData":[OSD([subQ9]),TDD([subQ43])]}),makeQuery(id+"F17.opExtrude","SWEPT_FACE",FACE,{"disambiguationData":[OSD([subQ33]),TDD([subQ42])]})]}),makeQuery(id+"F19.opExtrude","SWEPT_FACE",FACE,{"disambiguationData":[OSD([subQ12]),TDD([subQ48])]})]}),makeQuery(id+"F21.opExtrude","SWEPT_FACE",FACE,{"disambiguationData":[OSD([subQ10]),TDD([makeQuery(id+"F18.boolean.opBoolean","COPY",EDGE,{"derivedFrom":makeQuery(id+"F18.opExtrude","CAP_EDGE",EDGE,{"disambiguationData":[OSD([subQ10]),TDD([makeQuery(id+"F16.opExtrude","CAP_EDGE",EDGE,{"disambiguationData":[OSD([subQ10])],"isStart":false})])],"isStart":false})})])]})]}),makeQuery(id+"F23.opExtrude","SWEPT_FACE",FACE,{"disambiguationData":[OSD([subQ13]),TDD([subQ39])]})]}),makeQuery(id+"F25.opExtrude","SWEPT_FACE",FACE,{"disambiguationData":[OSD([subQ13]),TDD([subQ40])]})]}),makeQuery(id+"F27.opExtrude","SWEPT_FACE",FACE,{"disambiguationData":[OSD([subQ9]),TDD([subQ44])]})]}),makeQuery(id+"F29.opExtrude","SWEPT_FACE",FACE,{"disambiguationData":[OSD([subQ12]),TDD([subQ49])]})]}),makeQuery(id+"F31.opExtrude","SWEPT_FACE",FACE,{"disambiguationData":[OSD([subQ13]),TDD([subQ41])]})]}),makeQuery(id+"F33.opExtrude","SWEPT_FACE",FACE,{"disambiguationData":[OSD([subQ9]),TDD([subQ45])]})]}),makeQuery(id+"F36.opExtrude","SWEPT_FACE",FACE,{"disambiguationData":[OSD([subQ1]),TDD([subQ47])]})]}),makeQuery(id+"F39.opExtrude","SWEPT_FACE",FACE,{"disambiguationData":[OSD([subQ5]),TDD([makeQuery(id+"F18.boolean.opBoolean","COPY",EDGE,{"derivedFrom":makeQuery(id+"F18.opExtrude","CAP_EDGE",EDGE,{"disambiguationData":[OSD([subQ5]),TDD([makeQuery(id+"F16.opExtrude","CAP_EDGE",EDGE,{"disambiguationData":[OSD([subQ5])],"isStart":false})])],"isStart":false})})])]})]}),makeQuery(id+"F42.opExtrude","SWEPT_FACE",FACE,{"disambiguationData":[OSD([subQ12]),TDD([makeQuery(id+"F32.boolean.opBoolean","COPY",EDGE,{"derivedFrom":makeQuery(id+"F32.opExtrude","CAP_EDGE",EDGE,{"disambiguationData":[OSD([subQ12]),TDD([makeQuery(id+"F29.opExtrude","CAP_EDGE",EDGE,{"disambiguationData":[OSD([subQ12]),TDD([subQ49])],"isStart":false})])],"isStart":false})})])]}),makeQuery(id+"F42.opExtrude","SWEPT_FACE",FACE,{"disambiguationData":[OSD([subQ1]),TDD([makeQuery(id+"F36.opExtrude","CAP_EDGE",EDGE,{"disambiguationData":[OSD([subQ1]),TDD([subQ47])],"isStart":false})])]})]}),makeQuery(id+"F43.opExtrude","SWEPT_FACE",FACE,{"disambiguationData":[OSD([subQ25,subQ18,subQ16]),TDD([makeQuery(id+"F12.boolean.opBoolean","MERGE",EDGE,{"derivedFrom":[makeQuery(id+"F11.boolean.opBoolean","SPLIT",EDGE,{"disambiguationData":[TD([makeQuery(id+"F11.opExtrude","SWEPT_FACE",FACE,{"disambiguationData":[OSD([subQ16])]})])],"derivedFrom":subQ46}),makeQuery(id+"F12.opExtrude","SWEPT_EDGE",EDGE,{"disambiguationData":[OSD([subQ25,subQ18,subQ16]),TDD([makeQuery(id+"F11.opExtrude","CAP_VERTEX",VERTEX,{"disambiguationData":[OSD([subQ25,subQ18,subQ16])],"isStart":false})])]})]})])]}),makeQuery(id+"F43.opExtrude","SWEPT_FACE",FACE,{"disambiguationData":[OSD([subQ25,subQ18,subQ2]),TDD([makeQuery(id+"F13.boolean.opBoolean","MERGE",EDGE,{"derivedFrom":[makeQuery(id+"F11.boolean.opBoolean","SPLIT",EDGE,{"disambiguationData":[TD([makeQuery(id+"F11.opExtrude","SWEPT_FACE",FACE,{"disambiguationData":[OSD([subQ2])]})])],"derivedFrom":subQ46}),makeQuery(id+"F13.opExtrude","SWEPT_EDGE",EDGE,{"disambiguationData":[OSD([subQ25,subQ18,subQ2]),TDD([makeQuery(id+"F11.opExtrude","CAP_VERTEX",VERTEX,{"disambiguationData":[OSD([subQ25,subQ18,subQ2])],"isStart":false})])]})]})])]})]}),makeQuery(id+"F45.opExtrude","SWEPT_FACE",FACE,{"disambiguationData":[OSD([subQ9]),TDD([makeQuery(id+"F33.opExtrude","CAP_EDGE",EDGE,{"disambiguationData":[OSD([subQ9]),TDD([subQ45])],"isStart":false})])]}),makeQuery(id+"F45.opExtrude","SWEPT_FACE",FACE,{"disambiguationData":[OSD([subQ33]),TDD([makeQuery(id+"F40.boolean.opBoolean","COPY",EDGE,{"derivedFrom":makeQuery(id+"F40.opExtrude","CAP_EDGE",EDGE,{"disambiguationData":[OSD([subQ33]),TDD([makeQuery(id+"F38.boolean.opBoolean","COPY",EDGE,{"derivedFrom":makeQuery(id+"F38.opExtrude","CAP_EDGE",EDGE,{"disambiguationData":[OSD([subQ33]),TDD([makeQuery(id+"F17.opExtrude","CAP_EDGE",EDGE,{"disambiguationData":[OSD([subQ33]),TDD([subQ42])],"isStart":false})])],"isStart":false})})])],"isStart":false})})])]})]}),makeQuery(id+"F47.opExtrude","SWEPT_FACE",FACE,{"disambiguationData":[OSD([subQ13]),TDD([makeQuery(id+"F44.boolean.opBoolean","COPY",EDGE,{"derivedFrom":makeQuery(id+"F44.opExtrude","CAP_EDGE",EDGE,{"disambiguationData":[OSD([subQ13]),TDD([makeQuery(id+"F31.opExtrude","CAP_EDGE",EDGE,{"disambiguationData":[OSD([subQ13]),TDD([subQ41])],"isStart":false})])],"isStart":false})})])]}),makeQuery(id+"F47.opExtrude","SWEPT_FACE",FACE,{"disambiguationData":[OSD([subQ7]),TDD([makeQuery(id+"F44.boolean.opBoolean","COPY",EDGE,{"derivedFrom":makeQuery(id+"F44.opExtrude","CAP_EDGE",EDGE,{"disambiguationData":[OSD([subQ7]),TDD([makeQuery(id+"F37.boolean.opBoolean","COPY",EDGE,{"derivedFrom":makeQuery(id+"F37.opExtrude","CAP_EDGE",EDGE,{"disambiguationData":[OSD([subQ7]),TDD([makeQuery(id+"F16.opExtrude","CAP_EDGE",EDGE,{"disambiguationData":[OSD([subQ7])],"isStart":false})])],"isStart":false})})])],"isStart":false})})])]})]}),makeQuery(id+"F49.opExtrude","SWEPT_FACE",FACE,{"disambiguationData":[OSD([subQ27,subQ20]),TDD([makeQuery(id+"F3.boolean.opBoolean","MERGE",EDGE,{"derivedFrom":[makeQuery(id+"F2.opExtrude","CAP_EDGE",EDGE,{"disambiguationData":[OSD([subQ20]),TDD([subQ21])],"isStart":false}),makeQuery(id+"F3.opExtrude","SWEPT_EDGE",EDGE,{"disambiguationData":[OSD([subQ27,subQ20]),TDD([makeQuery(id+"F2.opExtrude","CAP_VERTEX",VERTEX,{"disambiguationData":[OSD([subQ27,subQ20]),TDD([subQ31])],"isStart":false})])]})]})])]})]}),makeQuery(id+"F50.opExtrude","SWEPT_FACE",FACE,{"disambiguationData":[OSD([subQ2,subQ33,subQ4]),TDD([makeQuery(id+"F40.boolean.opBoolean","MERGE",EDGE,{"derivedFrom":[makeQuery(id+"F38.boolean.opBoolean","MERGE",EDGE,{"derivedFrom":[makeQuery(id+"F16.boolean.opBoolean","SPLIT",EDGE,{"disambiguationData":[TD([makeQuery(id+"F8.boolean.opBoolean","COPY",FACE,{"derivedFrom":makeQuery(id+"F8.opExtrude","CAP_FACE",FACE,{"disambiguationData":[OSD([subQ24])],"isStart":false})})])],"derivedFrom":subQ35}),makeQuery(id+"F38.opExtrude","SWEPT_EDGE",EDGE,{"disambiguationData":[OSD([subQ2,subQ33,subQ4]),TDD([subQ38])]})]}),makeQuery(id+"F40.opExtrude","SWEPT_EDGE",EDGE,{"disambiguationData":[OSD([subQ2,subQ33,subQ4]),TDD([makeQuery(id+"F38.boolean.opBoolean","COPY",VERTEX,{"derivedFrom":makeQuery(id+"F38.opExtrude","CAP_VERTEX",VERTEX,{"disambiguationData":[OSD([subQ2,subQ33,subQ4]),TDD([subQ38])],"isStart":false})})])]})]})])]}),makeQuery(id+"F50.opExtrude","SWEPT_FACE",FACE,{"disambiguationData":[OSD([subQ2,subQ7,subQ0]),TDD([makeQuery(id+"F44.boolean.opBoolean","MERGE",EDGE,{"derivedFrom":[makeQuery(id+"F37.boolean.opBoolean","MERGE",EDGE,{"derivedFrom":[makeQuery(id+"F16.boolean.opBoolean","SPLIT",EDGE,{"disambiguationData":[TD([subQ37])],"derivedFrom":subQ35}),makeQuery(id+"F37.opExtrude","SWEPT_EDGE",EDGE,{"disambiguationData":[OSD([subQ2,subQ7,subQ0]),TDD([subQ36])]})]}),makeQuery(id+"F44.opExtrude","SWEPT_EDGE",EDGE,{"disambiguationData":[OSD([subQ2,subQ7,subQ0]),TDD([makeQuery(id+"F37.boolean.opBoolean","COPY",VERTEX,{"derivedFrom":makeQuery(id+"F37.opExtrude","CAP_VERTEX",VERTEX,{"disambiguationData":[OSD([subQ2,subQ7,subQ0]),TDD([subQ36])],"isStart":false})})])]})]})])]}),makeQuery(id+"F50.opExtrude","SWEPT_FACE",FACE,{"disambiguationData":[OSD([subQ2,subQ1,subQ0,subQ5,subQ4]),TDD([makeQuery(id+"F48.boolean.opBoolean","MERGE",EDGE,{"derivedFrom":[makeQuery(id+"F46.boolean.opBoolean","MERGE",EDGE,{"derivedFrom":[makeQuery(id+"F35.boolean.opBoolean","MERGE",EDGE,{"derivedFrom":[makeQuery(id+"F18.boolean.opBoolean","MERGE",EDGE,{"derivedFrom":[makeQuery(id+"F16.boolean.opBoolean","SPLIT",EDGE,{"disambiguationData":[TD([makeQuery(id+"F16.opExtrude","SWEPT_FACE",FACE,{"disambiguationData":[OSD([subQ1])]})])],"derivedFrom":subQ35}),makeQuery(id+"F18.opExtrude","SWEPT_EDGE",EDGE,{"disambiguationData":[OSD([subQ2,subQ5,subQ4]),TDD([subQ6])]})]}),makeQuery(id+"F35.opExtrude","SWEPT_EDGE",EDGE,{"disambiguationData":[OSD([subQ2,subQ1,subQ0]),TDD([subQ3])]})]}),makeQuery(id+"F46.opExtrude","SWEPT_EDGE",EDGE,{"disambiguationData":[OSD([subQ2,subQ5,subQ4]),TDD([makeQuery(id+"F39.opExtrude","CAP_VERTEX",VERTEX,{"disambiguationData":[OSD([subQ2,subQ5,subQ4]),TDD([makeQuery(id+"F18.boolean.opBoolean","COPY",VERTEX,{"derivedFrom":makeQuery(id+"F18.opExtrude","CAP_VERTEX",VERTEX,{"disambiguationData":[OSD([subQ2,subQ5,subQ4]),TDD([subQ6])],"isStart":false})})])],"isStart":false})])]})]}),makeQuery(id+"F48.opExtrude","SWEPT_EDGE",EDGE,{"disambiguationData":[OSD([subQ2,subQ1,subQ0]),TDD([makeQuery(id+"F42.opExtrude","CAP_VERTEX",VERTEX,{"disambiguationData":[OSD([subQ2,subQ1,subQ0]),TDD([makeQuery(id+"F36.opExtrude","CAP_VERTEX",VERTEX,{"disambiguationData":[OSD([subQ2,subQ1,subQ0]),TDD([makeQuery(id+"F35.boolean.opBoolean","COPY",VERTEX,{"derivedFrom":makeQuery(id+"F35.opExtrude","CAP_VERTEX",VERTEX,{"disambiguationData":[OSD([subQ2,subQ1,subQ0]),TDD([subQ3])],"isStart":false})})])],"isStart":false})])],"isStart":false})])]})]})])]})]});}
            fillet(context, id + "F53", {"entities" : qUnion([Q0]), "radius" : 3 * mm, "tangentPropagation" : true, "allowEdgeOverflow" : false});
        }
    });
